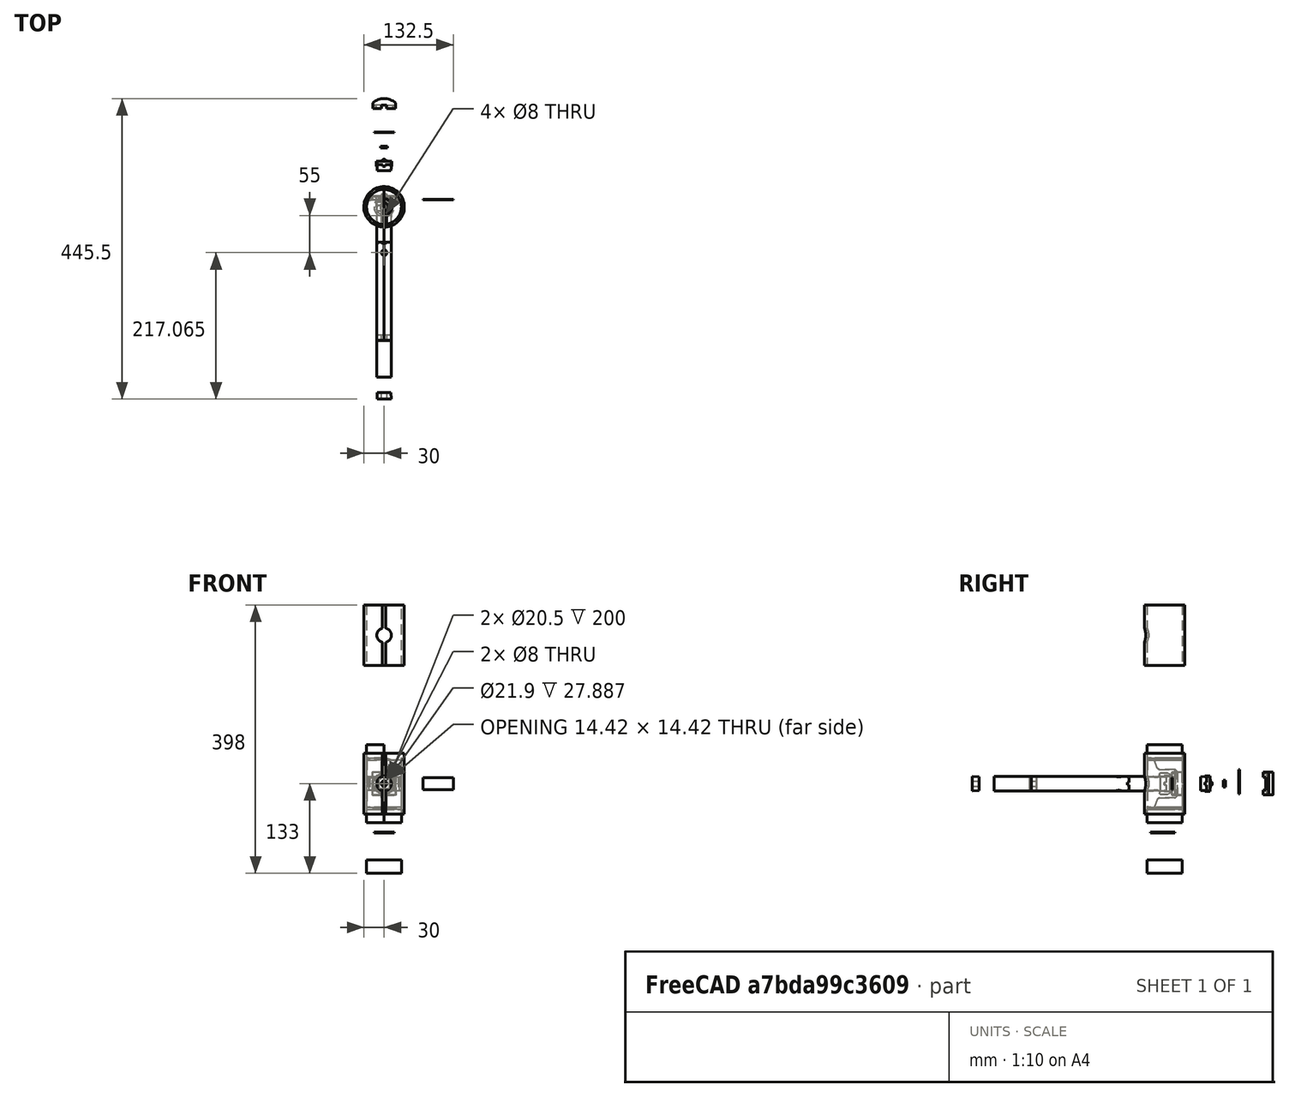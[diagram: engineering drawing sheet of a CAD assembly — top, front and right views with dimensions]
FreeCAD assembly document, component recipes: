
FREECAD ASSEMBLY — COMPONENT RECIPES ("Hammer")

This assembly document has 15 components, labeled P0..P14 below (a component is one placed body or linked part). 15 of them carry a construction recipe — the FreeCAD feature program that regenerates the part from scratch, quoted from this document or its linked companion documents; the rest are supplied as boundary geometry only. No exploded tour is included for this assembly.
NOTE — this tour is split across 2 documents so each fits a 32k-token context. This is document 1: the component sections continue in the remaining 1 document, each repeating the header above.
COMPONENT P0 — recipe-attached ("Body001_CutLink", modeled in this document).
Construction recipe (the document's own serialized feature program — sketch geometry with constraints, then the solid features built on it; lengths are millimeters unless a unit is written):

FEATURE [Sketcher::SketchObject] Sketch005  label="top_sens_base"
  FullyConstrained = true
  MapMode = 5
  Support = -> [XY_Plane]
  expr: Constraints[18] = <<Properties>>.Clearance
  expr: Constraints[1] = <<Properties>>.Head_ID
  expr: Constraints[3] = 34 - <<Properties>>.Clearance * 2
  expr: Constraints[6] = 10.5 + <<Properties>>.Clearance
  sketch-geometry (8):
    g0: Circle CenterX=0 CenterY=0 CenterZ=0 NormalX=0 NormalY=0 NormalZ=1 AngleXU=0 Radius=25.7
    g1: LineSegment StartX=-16.8 StartY=10.7 StartZ=0 EndX=16.8 EndY=10.7 EndZ=0
    g2: GeomPoint X=0 Y=10.7 Z=0
    g3: LineSegment StartX=-16.8 StartY=10.7 StartZ=0 EndX=-16.8 EndY=19.1836 EndZ=0
    g4: LineSegment StartX=16.8 StartY=10.7 StartZ=0 EndX=16.8 EndY=19.1836 EndZ=0
    g5: GeomPoint X=0 Y=25.7 Z=0
    g6: ArcOfCircle CenterX=0 CenterY=0 CenterZ=0 NormalX=0 NormalY=0 NormalZ=1 AngleXU=0 Radius=25.5 StartAngle=0.851542 EndAngle=2.29005
    g7: GeomPoint X=0 Y=25.5 Z=0
  constraints (19):
    c: Coincident(g0,g-1)
    c: Diameter(g0) = 51.4
    c: Horizontal(g1)
    c: DistanceX(g1,g1) = 33.6
    c: Symmetric(g1,g1,g2)
    c: PointOnObject(g2,g-2)
    c: DistanceY(g0,g2) = 10.7
    c: Coincident(g3,g1)
    c: Vertical(g3)
    c: Vertical(g4)
    c: Coincident(g4,g1)
    c: PointOnObject(g5,g0)
    c: PointOnObject(g5,g-2)
    c: Coincident(g6,g0)
    c: Coincident(g6,g3)
    c: Coincident(g6,g4)
    c: PointOnObject(g7,g6)
    c: PointOnObject(g7,g-2)
    c: DistanceY(g7,g5) = 0.2
FEATURE [PartDesign::Pad] Pad001  label="Top_Base"
  Direction = (0,0,1)
  Length = 16.8
  Length2 = 16.8
  Profile = -> Sketch005
  ReferenceAxis = -> Sketch005 [N_Axis]
  Type = 4
  expr: Length = <<Properties>>.Sensor_Diameter / 2 + 2 - <<Properties>>.Clearance
  expr: Length2 = <<Properties>>.Sensor_Diameter / 2 + 2 - <<Properties>>.Clearance
FEATURE [Sketcher::SketchObject] Sketch006
  FullyConstrained = true
  MapMode = 5
  Support = -> [XY_Plane]
  expr: Constraints[1] = Sketch003.Constraints[1]
  expr: Constraints[22] = Sketch003.Constraints[22]
  expr: Constraints[23] = Sketch003.Constraints[23]
  expr: Constraints[33] = Sketch003.Constraints[33]
  expr: Constraints[35] = Sketch003.Constraints[35]
  expr: Constraints[38] = Sketch003.Constraints[38]
  expr: Constraints[3] = Sketch003.Constraints[3]
  expr: Constraints[7] = Sketch003.Constraints[7]
  sketch-geometry (15):
    g0: Circle CenterX=0 CenterY=0 CenterZ=0 NormalX=0 NormalY=0 NormalZ=1 AngleXU=0 Radius=25.7
    g1: LineSegment StartX=-15.2 StartY=15.4669 StartZ=0 EndX=15.2 EndY=15.4669 EndZ=0
    g2: GeomPoint X=0 Y=15.4669 Z=0
    g3: LineSegment StartX=-23 StartY=11.4669 StartZ=0 EndX=23 EndY=11.4669 EndZ=0
    g4: GeomPoint X=0 Y=11.4669 Z=0
    g5: LineSegment StartX=-15.2 StartY=15.4669 StartZ=0 EndX=-21 EndY=11.4669 EndZ=0
    g6: LineSegment StartX=15.2 StartY=15.4669 StartZ=0 EndX=21 EndY=11.4669 EndZ=0
    g7: LineSegment StartX=21 StartY=11.4669 StartZ=0 EndX=23 EndY=11.4669 EndZ=0
    g8: LineSegment StartX=-21 StartY=11.4669 StartZ=0 EndX=-23 EndY=11.4669 EndZ=0
    g9: ArcOfCircle CenterX=0 CenterY=0 CenterZ=0 NormalX=0 NormalY=0 NormalZ=1 AngleXU=0 Radius=25.7 StartAngle=2.6791 EndAngle=2.80587
    g10: ArcOfCircle CenterX=0 CenterY=0 CenterZ=0 NormalX=0 NormalY=0 NormalZ=1 AngleXU=0 Radius=25.7 StartAngle=0.335723 EndAngle=0.462496
    g11: LineSegment StartX=-11 StartY=10.5 StartZ=0 EndX=-24.2652 EndY=8.46691 EndZ=0
    g12: LineSegment StartX=11 StartY=10.5 StartZ=0 EndX=24.2652 EndY=8.46691 EndZ=0
    g13: LineSegment StartX=11 StartY=10.5 StartZ=0 EndX=-11 EndY=10.5 EndZ=0
    g14: GeomPoint X=0 Y=10.5 Z=0
  constraints (40):
    c: Coincident(g0,g-1)
    c: Diameter(g0) = 51.4
    c: Horizontal(g1)
    c: DistanceX(g1,g1) = 30.4
    c: Symmetric(g1,g1,g2)
    c: PointOnObject(g2,g-2)
    c: Horizontal(g3)
    c: DistanceX(g3,g3) = 46
    c: Symmetric(g3,g3,g4)
    c: PointOnObject(g4,g-2)
    c: Coincident(g5,g1)
    c: PointOnObject(g5,g3)
    c: Coincident(g6,g1)
    c: PointOnObject(g6,g3)
    c: Coincident(g7,g6)
    c: PointOnObject(g7,g0)
    c: Horizontal(g7)
    c: Coincident(g8,g5)
    c: PointOnObject(g8,g0)
    c: Horizontal(g8)
    c: Equal(g8,g7)
    c: PointOnObject(g3,g0)
    c: DistanceY(g6,g1) = 4
    c: DistanceX(g6,g7) = 2
    c: Coincident(g9,g0)
    c: Coincident(g9,g8)
    c: Coincident(g10,g9)
    c: Coincident(g10,g7)
    c: Coincident(g13,g12)
    c: Coincident(g13,g11)
    c: Horizontal(g13)
    c: Coincident(g10,g12)
    c: Coincident(g9,g11)
    c: DistanceX(g12,g6) = 10
    c: Equal(g12,g11)
    c: DistanceY(g10,g7) = 3
    c: Symmetric(g13,g13,g14)
    c: PointOnObject(g14,g-2)
    c: DistanceY(g9,g14) = 10.5
    c: DistanceY(g9,g2) = 15.4669
FEATURE [PartDesign::Pocket] Pocket004
  BaseFeature = -> Pad001
  Direction = (0,0,-1)
  Length = 9.5
  Length2 = 9.5
  Profile = -> Sketch006
  ReferenceAxis = -> Sketch006 [N_Axis]
  Type = 4
FEATURE [PartDesign::Chamfer] Chamfer002
  Angle = 45
  Base = -> Pocket004 [Edge22,Edge12]
  BaseFeature = -> Pocket004
  ChamferType = 0
  FlipDirection = false
  Size = 0.3
  Size2 = 1
  SupportTransform = false
  UseAllEdges = false
FEATURE [Sketcher::SketchObject] Sketch007
  FullyConstrained = true
  MapMode = 5
  Placement = pos=(0,0,0) rot=(1,0,0;1.5708rad)
  Support = -> [XZ_Plane]
  expr: Constraints[11] = <<Properties>>.Sensor_Wire_Track_Width
  expr: Constraints[1] = <<Properties>>.Sensor_Diameter + 1
  expr: Constraints[27] = <<Properties>>.Sensor_Wire_Track_Width
  sketch-geometry (11):
    g0: Circle CenterX=0 CenterY=0 CenterZ=0 NormalX=0 NormalY=0 NormalZ=1 AngleXU=0 Radius=15.5
    g1: LineSegment StartX=-4 StartY=14.975 StartZ=0 EndX=-4 EndY=27.305 EndZ=0
    g2: LineSegment StartX=-4 StartY=27.305 StartZ=0 EndX=4 EndY=27.305 EndZ=0
    g3: LineSegment StartX=4 StartY=27.305 StartZ=0 EndX=4 EndY=14.975 EndZ=0
    g4: GeomPoint X=0 Y=27.305 Z=0
    g5: LineSegment StartX=-4 StartY=-14.975 StartZ=0 EndX=-4 EndY=-27.305 EndZ=0
    g6: LineSegment StartX=-4 StartY=-27.305 StartZ=0 EndX=4 EndY=-27.305 EndZ=0
    g7: LineSegment StartX=4 StartY=-27.305 StartZ=0 EndX=4 EndY=-14.975 EndZ=0
    g8: GeomPoint X=0 Y=-27.305 Z=0
    g9: ArcOfCircle CenterX=0 CenterY=0 CenterZ=0 NormalX=0 NormalY=0 NormalZ=1 AngleXU=0 Radius=15.5 StartAngle=1.83181 EndAngle=4.45137
    g10: ArcOfCircle CenterX=0 CenterY=0 CenterZ=0 NormalX=0 NormalY=0 NormalZ=1 AngleXU=0 Radius=15.5 StartAngle=4.97341 EndAngle=7.59296
  constraints (28):
    c: Coincident(g0,g-1)
    c: Diameter(g0) = 31
    c: PointOnObject(g1,g0)
    c: Vertical(g1)
    c: Coincident(g2,g1)
    c: Horizontal(g2)
    c: Coincident(g3,g2)
    c: PointOnObject(g3,g0)
    c: Vertical(g3)
    c: Symmetric(g2,g2,g4)
    c: PointOnObject(g4,g-2)
    c: DistanceX(g2,g2) = 8
    c: DistanceY(g3,g3) = 12.33
    c: Vertical(g5)
    c: Coincident(g6,g5)
    c: Horizontal(g6)
    c: Coincident(g7,g6)
    c: Vertical(g7)
    c: Symmetric(g6,g6,g8)
    c: PointOnObject(g8,g-2)
    c: Equal(g7,g3)
    c: Coincident(g9,g0)
    c: Coincident(g9,g1)
    c: Coincident(g9,g5)
    c: Coincident(g10,g9)
    c: Coincident(g10,g3)
    c: Coincident(g10,g7)
    c: DistanceX(g6,g6) = 8
FEATURE [PartDesign::Pocket] Pocket005
  BaseFeature = -> Chamfer002
  Direction = (0,1,2e-16)
  Length = 0
  Length2 = 5
  Offset = 0.4
  Profile = -> Sketch007
  ReferenceAxis = -> Sketch007 [N_Axis]
  Type = 3
  UpToFace = -> Chamfer002 [Face11]
FEATURE [PartDesign::Body] Body001  label="TopSensor"
  Group = -> [Sketch005,Pad001,Sketch006,Pocket004,Chamfer002,Sketch007,Pocket005]
  Origin = -> Origin
  Tip = -> Pocket005
COMPONENT P1 — recipe-attached ("Body002_CutLink", modeled in this document).
Construction recipe (the document's own serialized feature program — sketch geometry with constraints, then the solid features built on it; lengths are millimeters unless a unit is written):

FEATURE [Sketcher::SketchObject] Sketch009
  FullyConstrained = true
  MapMode = 5
  Support = -> [XY_Plane002]
  sketch-geometry (2):
    g0: Circle CenterX=0 CenterY=0 CenterZ=0 NormalX=0 NormalY=0 NormalZ=1 AngleXU=0 Radius=26
    g1: Circle CenterX=0 CenterY=0 CenterZ=0 NormalX=0 NormalY=0 NormalZ=1 AngleXU=0 Radius=30
  constraints (4):
    c: Coincident(g0,g-1)
    c: Coincident(g1,g0)
    c: Diameter(g0) = 52
    c: Diameter(g1) = 60
FEATURE [PartDesign::Pad] Pad002
  Direction = (0,0,1)
  Length = 45
  Length2 = 45
  Profile = -> Sketch009
  ReferenceAxis = -> Sketch009 [N_Axis]
  Type = 4
FEATURE [Sketcher::SketchObject] Sketch010
  FullyConstrained = true
  MapMode = 5
  Placement = pos=(0,0,0) rot=(1,0,0;1.5708rad)
  Support = -> [XZ_Plane002]
  expr: Constraints[1] = <<Properties>>.Handle_OD
  sketch-geometry (1):
    g0: Circle CenterX=0 CenterY=0 CenterZ=0 NormalX=0 NormalY=0 NormalZ=1 AngleXU=0 Radius=10.75
  constraints (2):
    c: Coincident(g0,g-1)
    c: Diameter(g0) = 21.5
FEATURE [PartDesign::Pocket] Pocket007
  BaseFeature = -> Pad002
  Direction = (0,1,2e-16)
  Length = 5
  Length2 = 5
  Profile = -> Sketch010
  ReferenceAxis = -> Sketch010 [N_Axis]
  Reversed = true
  Type = 1
FEATURE [Sketcher::SketchObject] Sketch027
  FullyConstrained = true
  MapMode = 5
  Placement = pos=(0,0,0) rot=(1,0,0;1.5708rad)
  Support = -> [XZ_Plane002]
  sketch-geometry (5):
    g0: LineSegment StartX=-2.5 StartY=-45 StartZ=0 EndX=-2.5 EndY=45 EndZ=0
    g1: LineSegment StartX=-2.5 StartY=45 StartZ=0 EndX=2.5 EndY=45 EndZ=0
    g2: LineSegment StartX=2.5 StartY=45 StartZ=0 EndX=2.5 EndY=-45 EndZ=0
    g3: LineSegment StartX=2.5 StartY=-45 StartZ=0 EndX=-2.5 EndY=-45 EndZ=0
    g4: GeomPoint X=0 Y=0 Z=0
  constraints (12):
    c: Coincident(g0,g1)
    c: Coincident(g1,g2)
    c: Coincident(g2,g3)
    c: Coincident(g3,g0)
    c: Horizontal(g1)
    c: Horizontal(g3)
    c: Vertical(g0)
    c: Vertical(g2)
    c: Symmetric(g1,g0,g4)
    c: Coincident(g4,g-1)
    c: DistanceX(g1,g1) = 5
    c: DistanceY(g2,g2) = 90
FEATURE [PartDesign::Pocket] Pocket012
  BaseFeature = -> Pocket007
  Direction = (0,1,2e-16)
  Length = 5
  Length2 = 5
  Profile = -> Sketch027
  ReferenceAxis = -> Sketch027 [N_Axis]
  Reversed = true
  Type = 1
FEATURE [PartDesign::Body] Body002  label="PVCHammerHeadShell"
  Group = -> [Sketch009,Pad002,Sketch010,Pocket007,Sketch027,Pocket012]
  Origin = -> Origin002
  Tip = -> Pocket012
COMPONENT P2 — recipe-attached ("Body003_CutLink", modeled in this document).
Construction recipe (the document's own serialized feature program — sketch geometry with constraints, then the solid features built on it; lengths are millimeters unless a unit is written):

FEATURE [Sketcher::SketchObject] Sketch011
  FullyConstrained = true
  MapMode = 5
  Placement = pos=(0,0,0) rot=(1,0,0;1.5708rad)
  Support = -> [XZ_Plane003]
  expr: Constraints[3] = <<Properties>>.Handle_ID
  sketch-geometry (2):
    g0: Circle CenterX=0 CenterY=0 CenterZ=0 NormalX=0 NormalY=0 NormalZ=1 AngleXU=0 Radius=10.625
    g1: Circle CenterX=0 CenterY=0 CenterZ=0 NormalX=0 NormalY=0 NormalZ=1 AngleXU=0 Radius=10.25
  constraints (4):
    c: Coincident(g0,g-1)
    c: Diameter(g0) = 21.25
    c: Coincident(g1,g0)
    c: Diameter(g1) = 20.5
FEATURE [PartDesign::Pad] Pad003
  Direction = (0,-1,-2e-16)
  Length = 200
  Length2 = 10
  Placement = pos=(0,0,0) rot=(1,0,0;1.5708rad)
  Profile = -> Sketch011
  ReferenceAxis = -> Sketch011 [N_Axis]
  Type = 0
FEATURE [Sketcher::SketchObject] Sketch018
  FullyConstrained = false
  MapMode = 5
  Support = -> [XY_Plane003]
  sketch-geometry (1):
    g0: Circle CenterX=0 CenterY=-15.4348 CenterZ=0 NormalX=0 NormalY=0 NormalZ=1 AngleXU=0 Radius=4
  constraints (2):
    c: PointOnObject(g0,g-2)
    c: Diameter(g0) = 8
FEATURE [PartDesign::Pocket] Pocket008
  BaseFeature = -> Pad003
  Direction = (0,0,-1)
  Length = 50
  Length2 = 50
  Placement = pos=(0,0,0) rot=(1,0,0;1.5708rad)
  Profile = -> Sketch018
  ReferenceAxis = -> Sketch018 [N_Axis]
  Type = 4
FEATURE [Sketcher::SketchObject] Sketch019
  FullyConstrained = true
  MapMode = 5
  Placement = pos=(0,0,0) rot=(1,0,0;1.5708rad)
  Support = -> [XZ_Plane003]
  sketch-geometry (17):
    g0: LineSegment StartX=12 StartY=-2 StartZ=0 EndX=12 EndY=2 EndZ=0
    g1: LineSegment StartX=12 StartY=2 StartZ=0 EndX=2 EndY=2 EndZ=0
    g2: LineSegment StartX=2 StartY=2 StartZ=0 EndX=2 EndY=12 EndZ=0
    g3: LineSegment StartX=2 StartY=12 StartZ=0 EndX=-2 EndY=12 EndZ=0
    g4: LineSegment StartX=-2 StartY=12 StartZ=0 EndX=-2 EndY=2 EndZ=0
    g5: LineSegment StartX=-2 StartY=2 StartZ=0 EndX=-12 EndY=2 EndZ=0
    g6: LineSegment StartX=-12 StartY=2 StartZ=0 EndX=-12 EndY=-2 EndZ=0
    g7: LineSegment StartX=-12 StartY=-2 StartZ=0 EndX=-2 EndY=-2 EndZ=0
    g8: LineSegment StartX=-2 StartY=-2 StartZ=0 EndX=-2 EndY=-12 EndZ=0
    g9: LineSegment StartX=-2 StartY=-12 StartZ=0 EndX=2 EndY=-12 EndZ=0
    g10: LineSegment StartX=2 StartY=-12 StartZ=0 EndX=2 EndY=-2 EndZ=0
    g11: LineSegment StartX=2 StartY=-2 StartZ=0 EndX=12 EndY=-2 EndZ=0
    g12: LineSegment StartX=-2 StartY=-2 StartZ=0 EndX=-2 EndY=2 EndZ=0
    g13: LineSegment StartX=-2 StartY=2 StartZ=0 EndX=2 EndY=2 EndZ=0
    g14: LineSegment StartX=2 StartY=2 StartZ=0 EndX=2 EndY=-2 EndZ=0
    g15: LineSegment StartX=2 StartY=-2 StartZ=0 EndX=-2 EndY=-2 EndZ=0
    g16: GeomPoint X=0 Y=0 Z=0
  constraints (46):
    c: Vertical(g0)
    c: Coincident(g1,g0)
    c: Horizontal(g1)
    c: Coincident(g2,g1)
    c: Vertical(g2)
    c: Coincident(g3,g2)
    c: Horizontal(g3)
    c: Coincident(g4,g3)
    c: Vertical(g4)
    c: Coincident(g5,g4)
    c: Horizontal(g5)
    c: Coincident(g6,g5)
    c: Vertical(g6)
    c: Horizontal(g7)
    c: Coincident(g8,g7)
    c: Vertical(g8)
    c: Horizontal(g9)
    c: Coincident(g10,g9)
    c: Vertical(g10)
    c: Coincident(g11,g10)
    c: Coincident(g11,g0)
    c: Horizontal(g11)
    c: Equal(g0,g3)
    c: Equal(g3,g6)
    c: Equal(g6,g9)
    c: Coincident(g6,g7)
    c: Coincident(g9,g8)
    c: Equal(g11,g7)
    c: Equal(g11,g1)
    c: Equal(g2,g4)
    c: Equal(g5,g10)
    c: Coincident(g12,g13)
    c: Coincident(g13,g14)
    c: Coincident(g14,g15)
    c: Coincident(g15,g12)
    c: Horizontal(g13)
    c: Horizontal(g15)
    c: Vertical(g12)
    c: Vertical(g14)
    c: Symmetric(g13,g12,g16)
    c: Coincident(g16,g-1)
    c: Coincident(g13,g1)
    c: Coincident(g7,g12)
    c: DistanceX(g13,g13) = 4
    c: DistanceY(g2,g2) = 10
    c: Equal(g10,g2)
FEATURE [PartDesign::Pocket] Pocket009
  BaseFeature = -> Pocket008
  Direction = (0,1,2e-16)
  Length = 3
  Length2 = 5
  Placement = pos=(0,0,0) rot=(1,0,0;1.5708rad)
  Profile = -> Sketch019
  ReferenceAxis = -> Sketch019 [N_Axis]
  Reversed = true
  Type = 0
FEATURE [PartDesign::Body] Body003  label="MetalHandle"
  Group = -> [Sketch011,Pad003,Sketch018,Pocket008,Sketch019,Pocket009]
  Origin = -> Origin003
  Placement = pos=(0,2.5,0) rot=(0,0,1;0rad)
  Tip = -> Pocket009
COMPONENT P3 — recipe-attached ("Body005_CutLink", modeled in this document).
Construction recipe (the document's own serialized feature program — sketch geometry with constraints, then the solid features built on it; lengths are millimeters unless a unit is written):

FEATURE [Sketcher::SketchObject] Sketch014
  FullyConstrained = true
  MapMode = 5
  Support = -> [XY_Plane005]
  sketch-geometry (5):
    g0: ArcOfCircle CenterX=0 CenterY=0 CenterZ=0 NormalX=0 NormalY=0 NormalZ=1 AngleXU=0 Radius=15 StartAngle=4.90695 EndAngle=10.801
    g1: LineSegment StartX=2.9 StartY=-14.717 StartZ=0 EndX=2.9 EndY=-20.717 EndZ=0
    g2: LineSegment StartX=2.9 StartY=-20.717 StartZ=0 EndX=-2.9 EndY=-20.717 EndZ=0
    g3: LineSegment StartX=-2.9 StartY=-20.717 StartZ=0 EndX=-2.9 EndY=-14.717 EndZ=0
    g4: LineSegment StartX=2.9 StartY=-14.717 StartZ=0 EndX=-2.9 EndY=-14.717 EndZ=0
  constraints (14):
    c: Coincident(g0,g-1)
    c: Radius(g0) = 15
    c: Coincident(g1,g0)
    c: Vertical(g1)
    c: Coincident(g2,g1)
    c: Horizontal(g2)
    c: Coincident(g3,g2)
    c: Coincident(g3,g0)
    c: Vertical(g3)
    c: DistanceX(g2,g2) = 5.8
    c: Coincident(g4,g0)
    c: Coincident(g4,g0)
    c: Horizontal(g4)
    c: DistanceY(g1,g1) = 6
FEATURE [PartDesign::Pad] Pad007
  Direction = (0,0,1)
  Length = 1
  Length2 = 10
  Profile = -> Sketch014
  ReferenceAxis = -> Sketch014 [N_Axis]
  Type = 0
FEATURE [PartDesign::Body] Body005  label="Sensor1"
  Group = -> [Sketch014,Pad007]
  Origin = -> Origin005
  Placement = pos=(0,0,37) rot=(0,0,1;0rad)
  Tip = -> Pad007
COMPONENT P4 — recipe-attached ("Body006_CutLink", modeled in this document).
Construction recipe (the document's own serialized feature program — sketch geometry with constraints, then the solid features built on it; lengths are millimeters unless a unit is written):

FEATURE [PartDesign::FeatureBase] Clone
  BaseFeature = -> Body005
FEATURE [PartDesign::Body] Body006  label="Sensor2"
  Group = -> [Clone]
  Origin = -> Origin006
  Placement = pos=(0,0,-37) rot=(0,1,0;3.14159rad)
  Tip = -> Clone
COMPONENT P5 — recipe-attached ("Body007_CutLink", modeled in this document).
Construction recipe (the document's own serialized feature program — sketch geometry with constraints, then the solid features built on it; lengths are millimeters unless a unit is written):

FEATURE [PartDesign::FeatureBase] Clone001
  BaseFeature = -> Body005
FEATURE [PartDesign::Body] Body007  label="Sensor3"
  Group = -> [Clone001]
  Origin = -> Origin007
  Placement = pos=(0,16,-4e-15) rot=(0,0.707107,-0.707107;3.14159rad)
  Tip = -> Clone001
COMPONENT P6 — recipe-attached ("Body008_CutLink", modeled in this document).
Construction recipe (the document's own serialized feature program — sketch geometry with constraints, then the solid features built on it; lengths are millimeters unless a unit is written):

FEATURE [Sketcher::SketchObject] Sketch015
  FullyConstrained = true
  MapMode = 5
  Support = -> [XY_Plane008]
  sketch-geometry (1):
    g0: Circle CenterX=0 CenterY=0 CenterZ=0 NormalX=0 NormalY=0 NormalZ=1 AngleXU=0 Radius=26
  constraints (2):
    c: Coincident(g0,g-1)
    c: Diameter(g0) = 52
FEATURE [PartDesign::Pad] Pad008
  Direction = (0,0,1)
  Length = 20
  Length2 = 10
  Profile = -> Sketch015
  ReferenceAxis = -> Sketch015 [N_Axis]
  Type = 0
FEATURE [PartDesign::Body] Body008  label="Foam1"
  Group = -> [Sketch015,Pad008]
  Origin = -> Origin008
  Placement = pos=(0,0,38) rot=(0,0,1;0rad)
  Tip = -> Pad008
COMPONENT P7 — recipe-attached ("Body009_CutLink", modeled in this document).
Construction recipe (the document's own serialized feature program — sketch geometry with constraints, then the solid features built on it; lengths are millimeters unless a unit is written):

FEATURE [PartDesign::FeatureBase] Clone002
  BaseFeature = -> Body008
  Placement = pos=(0,0,38) rot=(0,0,1;0rad)
FEATURE [PartDesign::Body] Body009  label="Foam2"
  Group = -> [Clone002]
  Origin = -> Origin009
  Placement = pos=(0,0,0) rot=(1,0,0;3.14159rad)
  Tip = -> Clone002
COMPONENT P8 — recipe-attached ("Body010_CutLink", modeled in this document).
Construction recipe (the document's own serialized feature program — sketch geometry with constraints, then the solid features built on it; lengths are millimeters unless a unit is written):

FEATURE [Sketcher::SketchObject] Sketch016
  FullyConstrained = true
  MapMode = 5
  Support = -> [XY_Plane010]
  sketch-geometry (5):
    g0: LineSegment StartX=-22.5 StartY=-0.4 StartZ=0 EndX=-22.5 EndY=0.4 EndZ=0
    g1: LineSegment StartX=-22.5 StartY=0.4 StartZ=0 EndX=22.5 EndY=0.4 EndZ=0
    g2: LineSegment StartX=22.5 StartY=0.4 StartZ=0 EndX=22.5 EndY=-0.4 EndZ=0
    g3: LineSegment StartX=22.5 StartY=-0.4 StartZ=0 EndX=-22.5 EndY=-0.4 EndZ=0
    g4: GeomPoint X=0 Y=0 Z=0
  constraints (12):
    c: Coincident(g0,g1)
    c: Coincident(g1,g2)
    c: Coincident(g2,g3)
    c: Coincident(g3,g0)
    c: Horizontal(g1)
    c: Horizontal(g3)
    c: Vertical(g0)
    c: Vertical(g2)
    c: Symmetric(g1,g0,g4)
    c: Coincident(g4,g-1)
    c: DistanceX(g1,g1) = 45
    c: DistanceY(g2,g2) = 0.8
FEATURE [PartDesign::Pad] Pad009
  Direction = (0,0,1)
  Length = 9
  Length2 = 9
  Profile = -> Sketch016
  ReferenceAxis = -> Sketch016 [N_Axis]
  Type = 4
FEATURE [PartDesign::Body] Body010  label="ShimStock"
  Group = -> [Sketch016,Pad009]
  Origin = -> Origin010
  Placement = pos=(0,11,0) rot=(0,0,1;0rad)
  Tip = -> Pad009
COMPONENT P9 — recipe-attached ("Body011_CutLink", modeled in this document).
Construction recipe (the document's own serialized feature program — sketch geometry with constraints, then the solid features built on it; lengths are millimeters unless a unit is written):

FEATURE [Sketcher::SketchObject] Sketch017
  FullyConstrained = true
  MapMode = 5
  Placement = pos=(0,0,0) rot=(1,0,0;1.5708rad)
  Support = -> [XZ_Plane011]
  sketch-geometry (1):
    g0: Circle CenterX=0 CenterY=0 CenterZ=0 NormalX=0 NormalY=0 NormalZ=1 AngleXU=0 Radius=5
  constraints (2):
    c: Coincident(g0,g-1)
    c: Diameter(g0) = 10
FEATURE [PartDesign::Pad] Pad010
  Direction = (0,-1,-2e-16)
  Length = 3
  Length2 = 10
  Placement = pos=(0,0,0) rot=(1,0,0;1.5708rad)
  Profile = -> Sketch017
  ReferenceAxis = -> Sketch017 [N_Axis]
  Type = 0
FEATURE [PartDesign::Body] Body011  label="TopFoam"
  Group = -> [Sketch017,Pad010]
  Origin = -> Origin011
  Placement = pos=(0,15,0) rot=(0,0,1;0rad)
  Tip = -> Pad010
COMPONENT P10 — recipe-attached ("Body012_CutLink", modeled in this document).
Construction recipe (the document's own serialized feature program — sketch geometry with constraints, then the solid features built on it; lengths are millimeters unless a unit is written):

FEATURE [Sketcher::SketchObject] Sketch020
  FullyConstrained = true
  MapMode = 5
  Placement = pos=(0,0,0) rot=(1,0,0;1.5708rad)
  Support = -> [XZ_Plane012]
  expr: Constraints[43] = Sketch019.Constraints[43]
  expr: Constraints[44] = Sketch019.Constraints[44]
  expr: Constraints[77] = <<Properties>>.Clearance
  expr: Constraints[78] = <<Properties>>.Clearance
  expr: Constraints[79] = <<Properties>>.Clearance
  expr: Constraints[81] = (<<Properties>>.Handle_OD + 2) / 2 - <<Properties>>.Clearance
  sketch-geometry (29):
    g0: LineSegment StartX=12 StartY=-2 StartZ=0 EndX=12 EndY=2 EndZ=0
    g1: LineSegment StartX=12 StartY=2 StartZ=0 EndX=2 EndY=2 EndZ=0
    g2: LineSegment StartX=2 StartY=2 StartZ=0 EndX=2 EndY=12 EndZ=0
    g3: LineSegment StartX=2 StartY=12 StartZ=0 EndX=-2 EndY=12 EndZ=0
    g4: LineSegment StartX=-2 StartY=12 StartZ=0 EndX=-2 EndY=2 EndZ=0
    g5: LineSegment StartX=-2 StartY=2 StartZ=0 EndX=-12 EndY=2 EndZ=0
    g6: LineSegment StartX=-12 StartY=2 StartZ=0 EndX=-12 EndY=-2 EndZ=0
    g7: LineSegment StartX=-12 StartY=-2 StartZ=0 EndX=-2 EndY=-2 EndZ=0
    g8: LineSegment StartX=-2 StartY=-2 StartZ=0 EndX=-2 EndY=-12 EndZ=0
    g9: LineSegment StartX=-2 StartY=-12 StartZ=0 EndX=2 EndY=-12 EndZ=0
    g10: LineSegment StartX=2 StartY=-12 StartZ=0 EndX=2 EndY=-2 EndZ=0
    g11: LineSegment StartX=2 StartY=-2 StartZ=0 EndX=12 EndY=-2 EndZ=0
    g12: LineSegment StartX=-2 StartY=-2 StartZ=0 EndX=-2 EndY=2 EndZ=0
    g13: LineSegment StartX=-2 StartY=2 StartZ=0 EndX=2 EndY=2 EndZ=0
    g14: LineSegment StartX=2 StartY=2 StartZ=0 EndX=2 EndY=-2 EndZ=0
    g15: LineSegment StartX=2 StartY=-2 StartZ=0 EndX=-2 EndY=-2 EndZ=0
    g16: GeomPoint X=0 Y=0 Z=0
    g17: LineSegment StartX=-1.8 StartY=11.55 StartZ=0 EndX=-1.8 EndY=1.8 EndZ=0
    g18: LineSegment StartX=-1.8 StartY=1.8 StartZ=0 EndX=-11.55 EndY=1.8 EndZ=0
    g19: LineSegment StartX=-11.55 StartY=1.8 StartZ=0 EndX=-11.55 EndY=-1.8 EndZ=0
    g20: LineSegment StartX=-11.55 StartY=-1.8 StartZ=0 EndX=-1.8 EndY=-1.8 EndZ=0
    g21: LineSegment StartX=-1.8 StartY=-1.8 StartZ=0 EndX=-1.8 EndY=-11.55 EndZ=0
    g22: LineSegment StartX=-1.8 StartY=-11.55 StartZ=0 EndX=1.8 EndY=-11.55 EndZ=0
    g23: LineSegment StartX=1.8 StartY=-11.55 StartZ=0 EndX=1.8 EndY=-1.8 EndZ=0
    g24: LineSegment StartX=1.8 StartY=-1.8 StartZ=0 EndX=11.55 EndY=-1.8 EndZ=0
    g25: LineSegment StartX=11.55 StartY=-1.8 StartZ=0 EndX=11.55 EndY=1.8 EndZ=0
    g26: LineSegment StartX=11.55 StartY=1.8 StartZ=0 EndX=1.8 EndY=1.8 EndZ=0
    g27: LineSegment StartX=1.8 StartY=1.8 StartZ=0 EndX=1.8 EndY=11.55 EndZ=0
    g28: LineSegment StartX=1.8 StartY=11.55 StartZ=0 EndX=-1.8 EndY=11.55 EndZ=0
  constraints (82):
    c: Vertical(g0)
    c: Coincident(g1,g0)
    c: Horizontal(g1)
    c: Coincident(g2,g1)
    c: Vertical(g2)
    c: Coincident(g3,g2)
    c: Horizontal(g3)
    c: Coincident(g4,g3)
    c: Vertical(g4)
    c: Coincident(g5,g4)
    c: Horizontal(g5)
    c: Coincident(g6,g5)
    c: Vertical(g6)
    c: Horizontal(g7)
    c: Coincident(g8,g7)
    c: Vertical(g8)
    c: Horizontal(g9)
    c: Coincident(g10,g9)
    c: Vertical(g10)
    c: Coincident(g11,g10)
    c: Coincident(g11,g0)
    c: Horizontal(g11)
    c: Equal(g0,g3)
    c: Equal(g3,g6)
    c: Equal(g6,g9)
    c: Coincident(g6,g7)
    c: Coincident(g9,g8)
    c: Equal(g11,g7)
    c: Equal(g11,g1)
    c: Equal(g2,g4)
    c: Equal(g5,g10)
    c: Coincident(g12,g13)
    c: Coincident(g13,g14)
    c: Coincident(g14,g15)
    c: Coincident(g15,g12)
    c: Horizontal(g13)
    c: Horizontal(g15)
    c: Vertical(g12)
    c: Vertical(g14)
    c: Symmetric(g13,g12,g16)
    c: Coincident(g16,g-1)
    c: Coincident(g13,g1)
    c: Coincident(g7,g12)
    c: DistanceX(g13,g13) = 4
    c: DistanceY(g2,g2) = 10
    c: Equal(g10,g2)
    c: Vertical(g17)
    c: Coincident(g18,g17)
    c: Horizontal(g18)
    c: Coincident(g19,g18)
    c: Vertical(g19)
    c: Coincident(g20,g19)
    c: Horizontal(g20)
    c: Coincident(g21,g20)
    c: Vertical(g21)
    c: Coincident(g22,g21)
    c: Horizontal(g22)
    c: Coincident(g23,g22)
    c: Vertical(g23)
    c: Coincident(g24,g23)
    c: Horizontal(g24)
    c: Coincident(g25,g24)
    c: Vertical(g25)
    c: Coincident(g26,g25)
    c: Horizontal(g26)
    c: Coincident(g27,g26)
    c: Vertical(g27)
    c: Coincident(g28,g27)
    c: Coincident(g28,g17)
    c: Horizontal(g28)
    c: Equal(g26,g18)
    c: Equal(g27,g17)
    c: Equal(g26,g24)
    c: Equal(g20,g24)
    c: Equal(g21,g23)
    c: Equal(g23,g27)
    c: Equal(g22,g25)
    c: DistanceX(g26,g1) = 0.2
    c: DistanceY(g26,g1) = 0.2
    c: DistanceY(g0,g24) = 0.2
    c: Equal(g23,g24)
    c: DistanceX(g16,g25) = 11.55
FEATURE [PartDesign::Pad] Pad011
  Direction = (0,-1,2e-16)
  Length = 2.8
  Length2 = 10
  Placement = pos=(0,0,0) rot=(1,0,0;1.5708rad)
  Profile = -> Sketch020
  ReferenceAxis = -> Sketch020 [N_Axis]
  Type = 0
FEATURE [Sketcher::SketchObject] Sketch021
  FullyConstrained = true
  MapMode = 5
  Placement = pos=(0,0,0) rot=(1,0,0;1.5708rad)
  Support = -> [XZ_Plane012]
  expr: Constraints[53] = Sketch020.Constraints[43]
  expr: Constraints[54] = Sketch020.Constraints[44]
  expr: Constraints[87] = Sketch020.Constraints[77]
  expr: Constraints[88] = Sketch020.Constraints[78]
  expr: Constraints[89] = Sketch020.Constraints[79]
  expr: Constraints[91] = Sketch020.Constraints[81]
  sketch-geometry (34):
    g0: LineSegment StartX=11.55 StartY=11.55 StartZ=0 EndX=11.55 EndY=-11.55 EndZ=0
    g1: LineSegment StartX=11.55 StartY=-11.55 StartZ=0 EndX=-11.55 EndY=-11.55 EndZ=0
    g2: LineSegment StartX=-11.55 StartY=-11.55 StartZ=0 EndX=-11.55 EndY=11.55 EndZ=0
    g3: LineSegment StartX=-11.55 StartY=11.55 StartZ=0 EndX=11.55 EndY=11.55 EndZ=0
    g4: GeomPoint X=0 Y=0 Z=0
    g5: LineSegment StartX=12 StartY=-2 StartZ=0 EndX=12 EndY=2 EndZ=0
    g6: LineSegment StartX=12 StartY=2 StartZ=0 EndX=2 EndY=2 EndZ=0
    g7: LineSegment StartX=2 StartY=2 StartZ=0 EndX=2 EndY=12 EndZ=0
    g8: LineSegment StartX=2 StartY=12 StartZ=0 EndX=-2 EndY=12 EndZ=0
    g9: LineSegment StartX=-2 StartY=12 StartZ=0 EndX=-2 EndY=2 EndZ=0
    g10: LineSegment StartX=-2 StartY=2 StartZ=0 EndX=-12 EndY=2 EndZ=0
    g11: LineSegment StartX=-12 StartY=2 StartZ=0 EndX=-12 EndY=-2 EndZ=0
    g12: LineSegment StartX=-12 StartY=-2 StartZ=0 EndX=-2 EndY=-2 EndZ=0
    g13: LineSegment StartX=-2 StartY=-2 StartZ=0 EndX=-2 EndY=-12 EndZ=0
    g14: LineSegment StartX=-2 StartY=-12 StartZ=0 EndX=2 EndY=-12 EndZ=0
    g15: LineSegment StartX=2 StartY=-12 StartZ=0 EndX=2 EndY=-2 EndZ=0
    g16: LineSegment StartX=2 StartY=-2 StartZ=0 EndX=12 EndY=-2 EndZ=0
    g17: LineSegment StartX=-2 StartY=-2 StartZ=0 EndX=-2 EndY=2 EndZ=0
    g18: LineSegment StartX=-2 StartY=2 StartZ=0 EndX=2 EndY=2 EndZ=0
    g19: LineSegment StartX=2 StartY=2 StartZ=0 EndX=2 EndY=-2 EndZ=0
    g20: LineSegment StartX=2 StartY=-2 StartZ=0 EndX=-2 EndY=-2 EndZ=0
    g21: GeomPoint X=0 Y=0 Z=0
    g22: LineSegment StartX=-1.8 StartY=11.55 StartZ=0 EndX=-1.8 EndY=1.8 EndZ=0
    g23: LineSegment StartX=-1.8 StartY=1.8 StartZ=0 EndX=-11.55 EndY=1.8 EndZ=0
    g24: LineSegment StartX=-11.55 StartY=1.8 StartZ=0 EndX=-11.55 EndY=-1.8 EndZ=0
    g25: LineSegment StartX=-11.55 StartY=-1.8 StartZ=0 EndX=-1.8 EndY=-1.8 EndZ=0
    g26: LineSegment StartX=-1.8 StartY=-1.8 StartZ=0 EndX=-1.8 EndY=-11.55 EndZ=0
    g27: LineSegment StartX=-1.8 StartY=-11.55 StartZ=0 EndX=1.8 EndY=-11.55 EndZ=0
    g28: LineSegment StartX=1.8 StartY=-11.55 StartZ=0 EndX=1.8 EndY=-1.8 EndZ=0
    g29: LineSegment StartX=1.8 StartY=-1.8 StartZ=0 EndX=11.55 EndY=-1.8 EndZ=0
    g30: LineSegment StartX=11.55 StartY=-1.8 StartZ=0 EndX=11.55 EndY=1.8 EndZ=0
    g31: LineSegment StartX=11.55 StartY=1.8 StartZ=0 EndX=1.8 EndY=1.8 EndZ=0
    g32: LineSegment StartX=1.8 StartY=1.8 StartZ=0 EndX=1.8 EndY=11.55 EndZ=0
    g33: LineSegment StartX=1.8 StartY=11.55 StartZ=0 EndX=-1.8 EndY=11.55 EndZ=0
  constraints (94):
    c: Coincident(g0,g1)
    c: Coincident(g1,g2)
    c: Coincident(g2,g3)
    c: Coincident(g3,g0)
    c: Horizontal(g1)
    c: Horizontal(g3)
    c: Vertical(g0)
    c: Vertical(g2)
    c: Symmetric(g1,g0,g4)
    c: Coincident(g4,g-1)
    c: Vertical(g5)
    c: Coincident(g6,g5)
    c: Horizontal(g6)
    c: Coincident(g7,g6)
    c: Vertical(g7)
    c: Coincident(g8,g7)
    c: Horizontal(g8)
    c: Coincident(g9,g8)
    c: Vertical(g9)
    c: Coincident(g10,g9)
    c: Horizontal(g10)
    c: Coincident(g11,g10)
    c: Vertical(g11)
    c: Horizontal(g12)
    c: Coincident(g13,g12)
    c: Vertical(g13)
    c: Horizontal(g14)
    c: Coincident(g15,g14)
    c: Vertical(g15)
    c: Coincident(g16,g15)
    c: Coincident(g16,g5)
    c: Horizontal(g16)
    c: Equal(g5,g8)
    c: Equal(g8,g11)
    c: Equal(g11,g14)
    c: Coincident(g11,g12)
    c: Coincident(g14,g13)
    c: Equal(g16,g12)
    c: Equal(g16,g6)
    c: Equal(g7,g9)
    c: Equal(g10,g15)
    c: Coincident(g17,g18)
    c: Coincident(g18,g19)
    c: Coincident(g19,g20)
    c: Coincident(g20,g17)
    c: Horizontal(g18)
    c: Horizontal(g20)
    c: Vertical(g17)
    c: Vertical(g19)
    c: Symmetric(g18,g17,g21)
    c: Coincident(g21,g-1)
    c: Coincident(g18,g6)
    c: Coincident(g12,g17)
    c: DistanceX(g18,g18) = 4
    c: DistanceY(g7,g7) = 10
    c: Equal(g15,g7)
    c: Vertical(g22)
    c: Coincident(g23,g22)
    c: Horizontal(g23)
    c: Coincident(g24,g23)
    c: Vertical(g24)
    c: Coincident(g25,g24)
    c: Horizontal(g25)
    c: Coincident(g26,g25)
    c: Vertical(g26)
    c: Coincident(g27,g26)
    c: Horizontal(g27)
    c: Coincident(g28,g27)
    c: Vertical(g28)
    c: Coincident(g29,g28)
    c: Horizontal(g29)
    c: Coincident(g30,g29)
    c: Vertical(g30)
    c: Coincident(g31,g30)
    c: Horizontal(g31)
    c: Coincident(g32,g31)
    c: Vertical(g32)
    c: Coincident(g33,g32)
    c: Coincident(g33,g22)
    c: Horizontal(g33)
    c: Equal(g31,g23)
    c: Equal(g32,g22)
    c: Equal(g31,g29)
    c: Equal(g25,g29)
    c: Equal(g26,g28)
    c: Equal(g28,g32)
    c: Equal(g27,g30)
    c: DistanceX(g31,g6) = 0.2
    c: DistanceY(g31,g6) = 0.2
    c: DistanceY(g5,g29) = 0.2
    c: Equal(g28,g29)
    c: DistanceX(g21,g30) = 11.55
    c: PointOnObject(g22,g3)
    c: PointOnObject(g23,g2)
FEATURE [PartDesign::Pad] Pad012
  BaseFeature = -> Pad011
  Direction = (0,-1,2e-16)
  Length = 5
  Length2 = 10
  Placement = pos=(0,0,0) rot=(1,0,0;1.5708rad)
  Profile = -> Sketch021
  ReferenceAxis = -> Sketch021 [N_Axis]
  Reversed = true
  Type = 0
FEATURE [Sketcher::SketchObject] Sketch023
  FullyConstrained = true
  MapMode = 5
  Placement = pos=(0,5,-2.2e-15) rot=(-1,0,0;1.5708rad)
  Support = -> [Pad012]
  sketch-geometry (1):
    g0: Circle CenterX=0 CenterY=0 CenterZ=0 NormalX=0 NormalY=0 NormalZ=1 AngleXU=0 Radius=2.5
  constraints (2):
    c: Coincident(g0,g-1)
    c: Diameter(g0) = 5
FEATURE [PartDesign::Pad] Pad013
  BaseFeature = -> Pad012
  Direction = (0,1,-2e-16)
  Length = 3
  Length2 = 10
  Placement = pos=(0,0,0) rot=(1,0,0;1.5708rad)
  Profile = -> Sketch023
  ReferenceAxis = -> Sketch023 [N_Axis]
  Type = 0
FEATURE [PartDesign::Fillet] Fillet
  Base = -> Pad013 [Edge51]
  BaseFeature = -> Pad013
  Placement = pos=(0,0,0) rot=(1,0,0;1.5708rad)
  Radius = 2
  SupportTransform = false
  UseAllEdges = false
FEATURE [PartDesign::Fillet] Fillet001
  Base = -> Fillet [Edge3]
  BaseFeature = -> Fillet
  Placement = pos=(0,0,0) rot=(1,0,0;1.5708rad)
  Radius = 7
  SupportTransform = false
  UseAllEdges = false
FEATURE [Sketcher::SketchObject] Sketch025
  FullyConstrained = true
  MapMode = 5
  Placement = pos=(0,0,0) rot=(1,0,0;1.5708rad)
  Support = -> [XZ_Plane012]
  expr: Constraints[1] = <<Properties>>.Handle_OD - <<Properties>>.Clearance * 2
  sketch-geometry (1):
    g0: Circle CenterX=0 CenterY=0 CenterZ=0 NormalX=0 NormalY=0 NormalZ=1 AngleXU=0 Radius=10.55
  constraints (2):
    c: Coincident(g0,g-1)
    c: Diameter(g0) = 21.1
FEATURE [PartDesign::Pad] Pad014
  BaseFeature = -> Fillet001
  Direction = (0,-1,2e-16)
  Length = 9
  Length2 = 10
  Placement = pos=(0,0,0) rot=(1,0,0;1.5708rad)
  Profile = -> Sketch025
  ReferenceAxis = -> Sketch025 [N_Axis]
  TaperAngle = -2
  Type = 0
FEATURE [PartDesign::Chamfer] Chamfer006
  Angle = 45
  Base = -> Pad014 [Edge15,Edge19,Edge10,Edge11]
  BaseFeature = -> Pad014
  ChamferType = 0
  FlipDirection = false
  Placement = pos=(0,0,0) rot=(1,0,0;1.5708rad)
  Size = 1
  Size2 = 1
  SupportTransform = false
  UseAllEdges = false
FEATURE [PartDesign::Body] Body012  label="Pusher"
  Group = -> [Sketch020,Pad011,Sketch021,Pad012,Sketch023,Pad013,Fillet,Fillet001,Sketch025,Pad014,Chamfer006]
  Origin = -> Origin012
  Placement = pos=(0,2.5,0) rot=(0,0,1;0rad)
  Tip = -> Chamfer006
COMPONENT P11 — recipe-attached ("Body013_CutLink", modeled in this document).
Construction recipe (the document's own serialized feature program — sketch geometry with constraints, then the solid features built on it; lengths are millimeters unless a unit is written):

FEATURE [Sketcher::SketchObject] Sketch026
  FullyConstrained = true
  MapMode = 5
  Placement = pos=(0,0,0) rot=(1,0,0;1.5708rad)
  Support = -> [XZ_Plane013]
  expr: Constraints[1] = <<Properties>>.Handle_OD - 1
  sketch-geometry (2):
    g0: Circle CenterX=0 CenterY=0 CenterZ=0 NormalX=0 NormalY=0 NormalZ=1 AngleXU=0 Radius=10.25
    g1: Circle CenterX=0 CenterY=0 CenterZ=0 NormalX=0 NormalY=0 NormalZ=1 AngleXU=0 Radius=4
  constraints (4):
    c: Coincident(g0,g-1)
    c: Diameter(g0) = 20.5
    c: Coincident(g1,g0)
    c: Diameter(g1) = 8
FEATURE [PartDesign::Pad] Pad015
  Direction = (0,-1,-2e-16)
  Length = 10
  Length2 = 10
  Placement = pos=(0,0,0) rot=(1,0,0;1.5708rad)
  Profile = -> Sketch026
  ReferenceAxis = -> Sketch026 [N_Axis]
  Type = 0
FEATURE [PartDesign::Draft] Draft
  Angle = 2
  Base = -> Pad015 [Face1]
  BaseFeature = -> Pad015
  NeutralPlane = -> Pad015 [Face3]
  Placement = pos=(0,0,0) rot=(1,0,0;1.5708rad)
  SupportTransform = false
FEATURE [PartDesign::Body] Body013  label="WirePlug"
  Group = -> [Sketch026,Pad015,Draft]
  Origin = -> Origin013
  Placement = pos=(0,-190,0) rot=(0,0,1;0rad)
  Tip = -> Draft
COMPONENT P12 — recipe-attached ("Body_CutLink", modeled in this document).
Construction recipe (the document's own serialized feature program — sketch geometry with constraints, then the solid features built on it; lengths are millimeters unless a unit is written):

FEATURE [Sketcher::SketchObject] Sketch  label="base"
  FullyConstrained = true
  MapMode = 5
  Support = -> [XY_Plane001]
  expr: Constraints[1] = <<Properties>>.Head_ID
  sketch-geometry (1):
    g0: Circle CenterX=0 CenterY=0 CenterZ=0 NormalX=0 NormalY=0 NormalZ=1 AngleXU=0 Radius=25.7
  constraints (2):
    c: Coincident(g0,g-1)
    c: Diameter(g0) = 51.4
FEATURE [PartDesign::Pad] Pad  label="Base"
  Direction = (0,0,1)
  Length = 35
  Length2 = 35
  Profile = -> Sketch
  ReferenceAxis = -> Sketch [N_Axis]
  Type = 4
  expr: Length = <<Properties>>.Insert_Len / 2
  expr: Length2 = <<Properties>>.Insert_Len / 2
FEATURE [Sketcher::SketchObject] Sketch001  label="sensor_wire_slot"
  FullyConstrained = true
  MapMode = 5
  Support = -> [XY_Plane001]
  expr: Constraints[11] = <<Properties>>.Sensor_Wire_Track_Width
  expr: Constraints[1] = Sketch.Constraints[1]
  sketch-geometry (7):
    g0: Circle CenterX=0 CenterY=0 CenterZ=0 NormalX=0 NormalY=0 NormalZ=1 AngleXU=0 Radius=25.7
    g1: LineSegment StartX=-4 StartY=-25.3868 StartZ=0 EndX=-4 EndY=-14.4568 EndZ=0
    g2: LineSegment StartX=-4 StartY=-14.4568 StartZ=0 EndX=4 EndY=-14.4568 EndZ=0
    g3: LineSegment StartX=4 StartY=-14.4568 StartZ=0 EndX=4 EndY=-25.3868 EndZ=0
    g4: ArcOfCircle CenterX=0 CenterY=0 CenterZ=0 NormalX=0 NormalY=0 NormalZ=1 AngleXU=0 Radius=25.7 StartAngle=4.55611 EndAngle=4.86867
    g5: GeomPoint X=0 Y=-14.4568 Z=0
    g6: Circle CenterX=0 CenterY=0 CenterZ=0 NormalX=0 NormalY=0 NormalZ=1 AngleXU=0 Radius=15
  constraints (17):
    c: Coincident(g0,g-1)
    c: Diameter(g0) = 51.4
    c: Vertical(g1)
    c: Coincident(g2,g1)
    c: Horizontal(g2)
    c: Coincident(g3,g2)
    c: Vertical(g3)
    c: Coincident(g4,g0)
    c: Coincident(g4,g1)
    c: Coincident(g4,g3)
    c: PointOnObject(g3,g0)
    c: DistanceX(g2,g2) = 8
    c: Symmetric(g2,g2,g5)
    c: PointOnObject(g5,g-2)
    c: Coincident(g6,g4)
    c: Diameter(g6) = 30
    c: PointOnObject(g2,g6)
FEATURE [PartDesign::Pocket] Pocket  label="Sensor_Wire_Slot"
  BaseFeature = -> Pad
  Direction = (0,0,-1)
  Length = 35
  Length2 = 35
  Profile = -> Sketch001
  ReferenceAxis = -> Sketch001 [N_Axis]
  Type = 4
  expr: Length = <<Properties>>.Insert_Len / 2
  expr: Length2 = <<Properties>>.Insert_Len / 2
FEATURE [Sketcher::SketchObject] Sketch002  label="handle_hole"
  FullyConstrained = true
  MapMode = 5
  Placement = pos=(0,0,0) rot=(1,0,0;1.5708rad)
  Support = -> [XZ_Plane001]
  expr: Constraints[1] = <<Properties>>.Handle_OD + <<Properties>>.Clearance * 2
  sketch-geometry (1):
    g0: Circle CenterX=0 CenterY=0 CenterZ=0 NormalX=0 NormalY=0 NormalZ=1 AngleXU=0 Radius=10.95
  constraints (2):
    c: Coincident(g0,g-1)
    c: Diameter(g0) = 21.9
FEATURE [PartDesign::Pocket] Pocket001  label="Handle_hole"
  BaseFeature = -> Pocket
  Direction = (0,1,2e-16)
  Length = 25.7
  Length2 = 25.7
  Profile = -> Sketch002
  ReferenceAxis = -> Sketch002 [N_Axis]
  Type = 4
  expr: Length = <<Properties>>.Head_ID / 2
  expr: Length2 = <<Properties>>.Head_ID / 2
FEATURE [Sketcher::SketchObject] Sketch004  label="top_sensor_hole"
  FullyConstrained = true
  MapMode = 5
  Placement = pos=(0,0,0) rot=(0.57735,0.57735,0.57735;2.0944rad)
  Support = -> [YZ_Plane001]
  expr: Constraints[20] = <<Properties>>.Head_ID
  expr: Constraints[7] = <<Properties>>.Sensor_Diameter + 4
  sketch-geometry (9):
    g0: LineSegment StartX=-25.7 StartY=-17 StartZ=0 EndX=-25.7 EndY=17 EndZ=0
    g1: LineSegment StartX=25.7 StartY=17 StartZ=0 EndX=25.7 EndY=-17 EndZ=0
    g2: LineSegment StartX=25.7 StartY=-17 StartZ=0 EndX=-25.7 EndY=-17 EndZ=0
    g3: GeomPoint X=0 Y=0 Z=0
    g4: LineSegment StartX=10.5 StartY=17 StartZ=0 EndX=25.7 EndY=17 EndZ=0
    g5: LineSegment StartX=25.7 StartY=17 StartZ=0 EndX=25.7 EndY=-17 EndZ=0
    g6: LineSegment StartX=25.7 StartY=-17 StartZ=0 EndX=10.5 EndY=-17 EndZ=0
    g7: LineSegment StartX=10.5 StartY=-17 StartZ=0 EndX=10.5 EndY=17 EndZ=0
    g8: LineSegment StartX=-25.7 StartY=17 StartZ=0 EndX=25.7 EndY=17 EndZ=0
  constraints (23):
    c: Coincident(g1,g2)
    c: Coincident(g2,g0)
    c: Horizontal(g2)
    c: Vertical(g0)
    c: Vertical(g1)
    c: Symmetric(g1,g0,g3)
    c: Coincident(g3,g-1)
    c: DistanceY(g1,g1) = 34
    c: Coincident(g4,g5)
    c: Coincident(g5,g6)
    c: Coincident(g6,g7)
    c: Horizontal(g4)
    c: Horizontal(g6)
    c: Vertical(g5)
    c: Vertical(g7)
    c: PointOnObject(g5,g2)
    c: Coincident(g7,g4)
    c: Coincident(g8,g0)
    c: Coincident(g8,g1)
    c: Horizontal(g8)
    c: DistanceX(g8,g8) = 51.4
    c: Coincident(g4,g1)
    c: DistanceX(g3,g4) = 10.5
FEATURE [PartDesign::Pocket] Pocket002  label="Top_Sensor_Hole"
  BaseFeature = -> Pocket001
  Direction = (-1,2e-16,-3e-16)
  Length = 17
  Length2 = 17
  Profile = -> Sketch004
  ReferenceAxis = -> Sketch004 [N_Axis]
  Type = 4
  expr: Length = <<Properties>>.Sensor_Diameter / 2 + 2
  expr: Length2 = <<Properties>>.Sensor_Diameter / 2 + 2
FEATURE [PartDesign::Chamfer] Chamfer
  Angle = 70
  Base = -> Pocket002 [Edge30,Edge32]
  BaseFeature = -> Pocket002
  ChamferType = 2
  FlipDirection = false
  Size = 8
  Size2 = 1
  SupportTransform = false
  UseAllEdges = false
FEATURE [Sketcher::SketchObject] Sketch003  label="spring_plate_slot"
  FullyConstrained = true
  MapMode = 5
  Support = -> [XY_Plane001]
  expr: Constraints[1] = Sketch.Constraints[1]
  expr: Constraints[3] = <<Properties>>.Sensor_Diameter + <<Properties>>.Clearance * 2
  expr: Constraints[7] = <<Properties>>.Spring_Plate_Len
  sketch-geometry (15):
    g0: Circle CenterX=0 CenterY=0 CenterZ=0 NormalX=0 NormalY=0 NormalZ=1 AngleXU=0 Radius=25.7
    g1: LineSegment StartX=-15.2 StartY=15.4669 StartZ=0 EndX=15.2 EndY=15.4669 EndZ=0
    g2: GeomPoint X=0 Y=15.4669 Z=0
    g3: LineSegment StartX=-23 StartY=11.4669 StartZ=0 EndX=23 EndY=11.4669 EndZ=0
    g4: GeomPoint X=0 Y=11.4669 Z=0
    g5: LineSegment StartX=-15.2 StartY=15.4669 StartZ=0 EndX=-21 EndY=11.4669 EndZ=0
    g6: LineSegment StartX=15.2 StartY=15.4669 StartZ=0 EndX=21 EndY=11.4669 EndZ=0
    g7: LineSegment StartX=21 StartY=11.4669 StartZ=0 EndX=23 EndY=11.4669 EndZ=0
    g8: LineSegment StartX=-21 StartY=11.4669 StartZ=0 EndX=-23 EndY=11.4669 EndZ=0
    g9: ArcOfCircle CenterX=0 CenterY=0 CenterZ=0 NormalX=0 NormalY=0 NormalZ=1 AngleXU=0 Radius=25.7 StartAngle=2.6791 EndAngle=2.80587
    g10: ArcOfCircle CenterX=0 CenterY=0 CenterZ=0 NormalX=0 NormalY=0 NormalZ=1 AngleXU=0 Radius=25.7 StartAngle=0.335723 EndAngle=0.462496
    g11: LineSegment StartX=-11 StartY=10.5 StartZ=0 EndX=-24.2652 EndY=8.46691 EndZ=0
    g12: LineSegment StartX=11 StartY=10.5 StartZ=0 EndX=24.2652 EndY=8.46691 EndZ=0
    g13: LineSegment StartX=11 StartY=10.5 StartZ=0 EndX=-11 EndY=10.5 EndZ=0
    g14: GeomPoint X=0 Y=10.5 Z=0
  constraints (39):
    c: Coincident(g0,g-1)
    c: Diameter(g0) = 51.4
    c: Horizontal(g1)
    c: DistanceX(g1,g1) = 30.4
    c: Symmetric(g1,g1,g2)
    c: PointOnObject(g2,g-2)
    c: Horizontal(g3)
    c: DistanceX(g3,g3) = 46
    c: Symmetric(g3,g3,g4)
    c: PointOnObject(g4,g-2)
    c: Coincident(g5,g1)
    c: PointOnObject(g5,g3)
    c: Coincident(g6,g1)
    c: PointOnObject(g6,g3)
    c: Coincident(g7,g6)
    c: PointOnObject(g7,g0)
    c: Horizontal(g7)
    c: Coincident(g8,g5)
    c: PointOnObject(g8,g0)
    c: Horizontal(g8)
    c: Equal(g8,g7)
    c: PointOnObject(g3,g0)
    c: DistanceY(g6,g1) = 4
    c: DistanceX(g6,g7) = 2
    c: Coincident(g9,g0)
    c: Coincident(g9,g8)
    c: Coincident(g10,g9)
    c: Coincident(g10,g7)
    c: Coincident(g13,g12)
    c: Coincident(g13,g11)
    c: Horizontal(g13)
    c: Coincident(g10,g12)
    c: Coincident(g9,g11)
    c: DistanceX(g12,g6) = 10
    c: Equal(g12,g11)
    c: DistanceY(g10,g7) = 3
    c: Symmetric(g13,g13,g14)
    c: PointOnObject(g14,g-2)
    c: DistanceY(g9,g14) = 10.5
FEATURE [PartDesign::Pocket] Pocket003  label="Spring_Plate_Slot"
  BaseFeature = -> Chamfer
  Direction = (0,0,-1)
  Length = 10
  Length2 = 10
  Profile = -> Sketch003
  ReferenceAxis = -> Sketch003 [N_Axis]
  Type = 4
FEATURE [PartDesign::Chamfer] Chamfer001
  Angle = 45
  Base = -> Pocket003 [Edge43,Edge46,Edge45,Edge47,Edge44,Edge42]
  BaseFeature = -> Pocket003
  ChamferType = 0
  FlipDirection = false
  Size = 0.5
  Size2 = 1
  SupportTransform = false
  UseAllEdges = false
FEATURE [Sketcher::SketchObject] Sketch008
  FullyConstrained = true
  MapMode = 5
  Placement = pos=(0,0,0) rot=(0.57735,0.57735,0.57735;2.0944rad)
  Support = -> [YZ_Plane001]
  expr: Constraints[16] = <<Properties>>.Sensor_Diameter + 2
  sketch-geometry (14):
    g0: LineSegment StartX=15.5 StartY=21 StartZ=0 EndX=15.5 EndY=-21 EndZ=0
    g1: LineSegment StartX=15.5 StartY=-21 StartZ=0 EndX=-19.02 EndY=-21 EndZ=0
    g2: LineSegment StartX=-19.02 StartY=-21 StartZ=0 EndX=-19.02 EndY=-16 EndZ=0
    g3: LineSegment StartX=-19.02 StartY=-16 StartZ=0 EndX=10.5 EndY=-16 EndZ=0
    g4: LineSegment StartX=10.5 StartY=-16 StartZ=0 EndX=10.5 EndY=16 EndZ=0
    g5: LineSegment StartX=10.5 StartY=16 StartZ=0 EndX=-19.02 EndY=16 EndZ=0
    g6: LineSegment StartX=-19.02 StartY=16 StartZ=0 EndX=-19.02 EndY=21 EndZ=0
    g7: LineSegment StartX=-19.02 StartY=21 StartZ=0 EndX=15.5 EndY=21 EndZ=0
    g8: GeomPoint X=10.5 Y=0 Z=0
    g9: GeomPoint X=15.5 Y=0 Z=0
    g10: GeomPoint X=15.5 Y=21 Z=0
    g11: GeomPoint X=15.5 Y=-21 Z=0
    g12: GeomPoint X=10.5 Y=16 Z=0
    g13: GeomPoint X=10.5 Y=-16 Z=0
  constraints (30):
    c: Vertical(g0)
    c: Horizontal(g1)
    c: Coincident(g2,g1)
    c: Vertical(g2)
    c: Coincident(g3,g2)
    c: Horizontal(g3)
    c: Vertical(g4)
    c: Horizontal(g5)
    c: Coincident(g6,g5)
    c: Vertical(g6)
    c: Coincident(g7,g6)
    c: Horizontal(g7)
    c: Symmetric(g10,g11,g9)
    c: Symmetric(g13,g12,g8)
    c: PointOnObject(g8,g-1)
    c: PointOnObject(g9,g-1)
    c: DistanceY(g13,g12) = 32
    c: DistanceY(g6,g6) = 5
    c: DistanceX(g8,g9) = 5
    c: DistanceX(g-1,g8) = 10.5
    c: DistanceX(g7,g10) = 34.52
    c: Coincident(g0,g10)
    c: Coincident(g7,g0)
    c: Coincident(g4,g12)
    c: Coincident(g5,g4)
    c: Coincident(g0,g11)
    c: Coincident(g4,g13)
    c: Coincident(g3,g4)
    c: Coincident(g1,g0)
    c: Equal(g3,g5)
FEATURE [PartDesign::Pocket] Pocket006
  BaseFeature = -> Chamfer001
  Direction = (-1,2e-16,-3e-16)
  Length = 4
  Length2 = 4
  Profile = -> Sketch008
  ReferenceAxis = -> Sketch008 [N_Axis]
  Type = 4
  expr: Length = <<Properties>>.Sensor_Wire_Track_Width / 2
  expr: Length2 = <<Properties>>.Sensor_Wire_Track_Width / 2
FEATURE [PartDesign::Chamfer] Chamfer003
  Angle = 65
  Base = -> Pocket006 [Edge148,Edge154]
  BaseFeature = -> Pocket006
  ChamferType = 2
  FlipDirection = false
  Size = 3
  Size2 = 1
  SupportTransform = false
  UseAllEdges = false
FEATURE [PartDesign::Chamfer] Chamfer004
  Angle = 45
  Base = -> Chamfer003 [Edge167,Edge85,Edge52,Edge56]
  BaseFeature = -> Chamfer003
  ChamferType = 0
  FlipDirection = false
  Size = 2
  Size2 = 1
  SupportTransform = false
  UseAllEdges = false
FEATURE [PartDesign::Chamfer] Chamfer005
  Angle = 45
  Base = -> Chamfer004 [Edge169,Edge38]
  BaseFeature = -> Chamfer004
  ChamferType = 1
  FlipDirection = false
  Size = 4
  Size2 = 3.999
  SupportTransform = false
  UseAllEdges = false
FEATURE [PartDesign::AdditiveCone] Cone
  Angle = 360
  AttacherType = Attacher::AttachEngine3D
  BaseFeature = -> Chamfer005
  Height = 1.5
  MapMode = 5
  Placement = pos=(0,0,35) rot=(0,0,1;0rad)
  Radius1 = 12
  Radius2 = 6
  Support = -> [Chamfer005]
FEATURE [PartDesign::AdditiveCone] Cone001
  Angle = 360
  AttacherType = Attacher::AttachEngine3D
  BaseFeature = -> Cone
  Height = 1.5
  MapMode = 5
  Placement = pos=(0,0,-35) rot=(1,0,0;3.14159rad)
  Radius1 = 12
  Radius2 = 6
  Support = -> [Cone]
FEATURE [Sketcher::SketchObject] Sketch022
  ExternalGeometry = -> [Cone001]
  FullyConstrained = true
  MapMode = 5
  Placement = pos=(2.3e-15,10.5,-35) rot=(-1,0,0;1.5708rad)
  Support = -> [Cone001]
  expr: Constraints[11] = <<Properties>>.Handle_OD + 2
  sketch-geometry (5):
    g0: LineSegment StartX=-11.75 StartY=-46.75 StartZ=0 EndX=-11.75 EndY=-23.25 EndZ=0
    g1: LineSegment StartX=-11.75 StartY=-23.25 StartZ=0 EndX=11.75 EndY=-23.25 EndZ=0
    g2: LineSegment StartX=11.75 StartY=-23.25 StartZ=0 EndX=11.75 EndY=-46.75 EndZ=0
    g3: LineSegment StartX=11.75 StartY=-46.75 StartZ=0 EndX=-11.75 EndY=-46.75 EndZ=0
    g4: GeomPoint X=-2.3e-15 Y=-35 Z=0
  constraints (12):
    c: Coincident(g0,g1)
    c: Coincident(g1,g2)
    c: Coincident(g2,g3)
    c: Coincident(g3,g0)
    c: Horizontal(g1)
    c: Horizontal(g3)
    c: Vertical(g0)
    c: Vertical(g2)
    c: Symmetric(g1,g0,g4)
    c: Coincident(g4,g-3)
    c: Equal(g2,g1)
    c: DistanceX(g1,g1) = 23.5
FEATURE [PartDesign::Pocket] Pocket010
  BaseFeature = -> Cone001
  Direction = (-2e-16,-1,2e-16)
  Length = 8
  Length2 = 5
  Placement = pos=(0,0,-35) rot=(1,0,0;3.14159rad)
  Profile = -> Sketch022
  ReferenceAxis = -> Sketch022 [N_Axis]
  Type = 0
FEATURE [Sketcher::SketchObject] Sketch024
  ExternalGeometry = -> [Cone001]
  FullyConstrained = true
  MapMode = 5
  Placement = pos=(6e-16,2.5,-35) rot=(-1,0,0;1.5708rad)
  Support = -> [Pocket010]
  expr: Constraints[11] = Sketch022.Constraints[11]
  expr: Constraints[54] = Sketch019.Constraints[43]
  expr: Constraints[55] = Sketch019.Constraints[44]
  sketch-geometry (34):
    g0: LineSegment StartX=-11.75 StartY=-46.75 StartZ=0 EndX=-11.75 EndY=-23.25 EndZ=0
    g1: LineSegment StartX=-11.75 StartY=-23.25 StartZ=0 EndX=11.75 EndY=-23.25 EndZ=0
    g2: LineSegment StartX=11.75 StartY=-23.25 StartZ=0 EndX=11.75 EndY=-46.75 EndZ=0
    g3: LineSegment StartX=11.75 StartY=-46.75 StartZ=0 EndX=-11.75 EndY=-46.75 EndZ=0
    g4: GeomPoint X=-2.4e-15 Y=-35 Z=0
    g5: LineSegment StartX=12 StartY=-37 StartZ=0 EndX=12 EndY=-33 EndZ=0
    g6: LineSegment StartX=12 StartY=-33 StartZ=0 EndX=2 EndY=-33 EndZ=0
    g7: LineSegment StartX=2 StartY=-33 StartZ=0 EndX=2 EndY=-23 EndZ=0
    g8: LineSegment StartX=2 StartY=-23 StartZ=0 EndX=-2 EndY=-23 EndZ=0
    g9: LineSegment StartX=-2 StartY=-23 StartZ=0 EndX=-2 EndY=-33 EndZ=0
    g10: LineSegment StartX=-2 StartY=-33 StartZ=0 EndX=-12 EndY=-33 EndZ=0
    g11: LineSegment StartX=-12 StartY=-33 StartZ=0 EndX=-12 EndY=-37 EndZ=0
    g12: LineSegment StartX=-12 StartY=-37 StartZ=0 EndX=-2 EndY=-37 EndZ=0
    g13: LineSegment StartX=-2 StartY=-37 StartZ=0 EndX=-2 EndY=-47 EndZ=0
    g14: LineSegment StartX=-2 StartY=-47 StartZ=0 EndX=2 EndY=-47 EndZ=0
    g15: LineSegment StartX=2 StartY=-47 StartZ=0 EndX=2 EndY=-37 EndZ=0
    g16: LineSegment StartX=2 StartY=-37 StartZ=0 EndX=12 EndY=-37 EndZ=0
    g17: LineSegment StartX=-2 StartY=-37 StartZ=0 EndX=-2 EndY=-33 EndZ=0
    g18: LineSegment StartX=-2 StartY=-33 StartZ=0 EndX=2 EndY=-33 EndZ=0
    g19: LineSegment StartX=2 StartY=-33 StartZ=0 EndX=2 EndY=-37 EndZ=0
    g20: LineSegment StartX=2 StartY=-37 StartZ=0 EndX=-2 EndY=-37 EndZ=0
    g21: GeomPoint X=0 Y=0 Z=0
    g22: LineSegment StartX=-2 StartY=-23.25 StartZ=0 EndX=2 EndY=-23.25 EndZ=0
    g23: LineSegment StartX=2 StartY=-23.25 StartZ=0 EndX=2 EndY=-33 EndZ=0
    g24: LineSegment StartX=2 StartY=-33 StartZ=0 EndX=11.75 EndY=-33 EndZ=0
    g25: LineSegment StartX=11.75 StartY=-33 StartZ=0 EndX=11.75 EndY=-37 EndZ=0
    g26: LineSegment StartX=11.75 StartY=-37 StartZ=0 EndX=2 EndY=-37 EndZ=0
    g27: LineSegment StartX=2 StartY=-37 StartZ=0 EndX=2 EndY=-46.75 EndZ=0
    g28: LineSegment StartX=2 StartY=-46.75 StartZ=0 EndX=-2 EndY=-46.75 EndZ=0
    g29: LineSegment StartX=-2 StartY=-46.75 StartZ=0 EndX=-2 EndY=-37 EndZ=0
    g30: LineSegment StartX=-2 StartY=-37 StartZ=0 EndX=-11.75 EndY=-37 EndZ=0
    g31: LineSegment StartX=-11.75 StartY=-37 StartZ=0 EndX=-11.75 EndY=-33 EndZ=0
    g32: LineSegment StartX=-11.75 StartY=-33 StartZ=0 EndX=-2 EndY=-33 EndZ=0
    g33: LineSegment StartX=-2 StartY=-33 StartZ=0 EndX=-2 EndY=-23.25 EndZ=0
  constraints (90):
    c: Coincident(g0,g1)
    c: Coincident(g1,g2)
    c: Coincident(g2,g3)
    c: Coincident(g3,g0)
    c: Horizontal(g1)
    c: Horizontal(g3)
    c: Vertical(g0)
    c: Vertical(g2)
    c: Symmetric(g1,g0,g4)
    c: Coincident(g4,g-3)
    c: Equal(g2,g1)
    c: DistanceX(g1,g1) = 23.5
    c: Vertical(g5)
    c: Coincident(g6,g5)
    c: Horizontal(g6)
    c: Coincident(g7,g6)
    c: Vertical(g7)
    c: Coincident(g8,g7)
    c: Horizontal(g8)
    c: Coincident(g9,g8)
    c: Vertical(g9)
    c: Coincident(g10,g9)
    c: Horizontal(g10)
    c: Coincident(g11,g10)
    c: Vertical(g11)
    c: Horizontal(g12)
    c: Coincident(g13,g12)
    c: Vertical(g13)
    c: Horizontal(g14)
    c: Coincident(g15,g14)
    c: Vertical(g15)
    c: Coincident(g16,g15)
    c: Coincident(g16,g5)
    c: Horizontal(g16)
    c: Equal(g5,g8)
    c: Equal(g8,g11)
    c: Equal(g11,g14)
    c: Coincident(g11,g12)
    c: Coincident(g14,g13)
    c: Equal(g16,g12)
    c: Equal(g16,g6)
    c: Equal(g7,g9)
    c: Equal(g10,g15)
    c: Coincident(g17,g18)
    c: Coincident(g18,g19)
    c: Coincident(g19,g20)
    c: Coincident(g20,g17)
    c: Horizontal(g18)
    c: Horizontal(g20)
    c: Vertical(g17)
    c: Vertical(g19)
    c: Coincident(g21,g-1)
    c: Coincident(g18,g6)
    c: Coincident(g12,g17)
    c: DistanceX(g18,g18) = 4
    c: DistanceY(g7,g7) = 10
    c: Equal(g15,g7)
    c: Symmetric(g6,g12,g4)
    c: PointOnObject(g22,g9)
    c: PointOnObject(g22,g1)
    c: Horizontal(g22)
    c: PointOnObject(g22,g7)
    c: Coincident(g23,g22)
    c: Coincident(g23,g6)
    c: Coincident(g24,g23)
    c: PointOnObject(g24,g2)
    c: Horizontal(g24)
    c: Coincident(g25,g24)
    c: PointOnObject(g25,g16)
    c: Vertical(g25)
    c: Coincident(g26,g25)
    c: Coincident(g26,g15)
    c: Coincident(g27,g26)
    c: PointOnObject(g27,g3)
    c: Vertical(g27)
    c: Coincident(g28,g27)
    c: PointOnObject(g28,g13)
    c: Horizontal(g28)
    c: Coincident(g29,g28)
    c: Coincident(g29,g12)
    c: Coincident(g30,g29)
    c: PointOnObject(g30,g0)
    c: Horizontal(g30)
    c: Coincident(g31,g30)
    c: PointOnObject(g31,g10)
    c: Vertical(g31)
    c: Coincident(g32,g31)
    c: Coincident(g32,g9)
    c: Coincident(g33,g32)
    c: Coincident(g33,g22)
FEATURE [PartDesign::Pocket] Pocket011
  BaseFeature = -> Pocket010
  Direction = (-2e-16,-1,2e-16)
  Length = 3
  Length2 = 5
  Placement = pos=(0,0,-35) rot=(1,0,0;3.14159rad)
  Profile = -> Sketch024
  ReferenceAxis = -> Sketch024 [N_Axis]
  Type = 0
FEATURE [PartDesign::Body] Body  label="HeadInstert"
  Group = -> [Sketch,Pad,Sketch001,Pocket,Sketch002,Pocket001,Sketch004,Pocket002,Chamfer,Sketch003,Pocket003,Chamfer001,Sketch008,Pocket006,Chamfer003,Chamfer004,Chamfer005,Cone,Cone001,Sketch022,Pocket010,Sketch024,Pocket011]
  Origin = -> Origin001
  Tip = -> Pocket011
COMPONENT P13 — recipe-attached ("Part", modeled in this document).
Construction recipe (the document's own serialized feature program — sketch geometry with constraints, then the solid features built on it; lengths are millimeters unless a unit is written):

FEATURE [Sketcher::SketchObject] Sketch  label="base"
  FullyConstrained = true
  MapMode = 5
  Support = -> [XY_Plane001]
  expr: Constraints[1] = <<Properties>>.Head_ID
  sketch-geometry (1):
    g0: Circle CenterX=0 CenterY=0 CenterZ=0 NormalX=0 NormalY=0 NormalZ=1 AngleXU=0 Radius=25.7
  constraints (2):
    c: Coincident(g0,g-1)
    c: Diameter(g0) = 51.4
FEATURE [PartDesign::Pad] Pad  label="Base"
  Direction = (0,0,1)
  Length = 35
  Length2 = 35
  Profile = -> Sketch
  ReferenceAxis = -> Sketch [N_Axis]
  Type = 4
  expr: Length = <<Properties>>.Insert_Len / 2
  expr: Length2 = <<Properties>>.Insert_Len / 2
FEATURE [Sketcher::SketchObject] Sketch001  label="sensor_wire_slot"
  FullyConstrained = true
  MapMode = 5
  Support = -> [XY_Plane001]
  expr: Constraints[11] = <<Properties>>.Sensor_Wire_Track_Width
  expr: Constraints[1] = Sketch.Constraints[1]
  sketch-geometry (7):
    g0: Circle CenterX=0 CenterY=0 CenterZ=0 NormalX=0 NormalY=0 NormalZ=1 AngleXU=0 Radius=25.7
    g1: LineSegment StartX=-4 StartY=-25.3868 StartZ=0 EndX=-4 EndY=-14.4568 EndZ=0
    g2: LineSegment StartX=-4 StartY=-14.4568 StartZ=0 EndX=4 EndY=-14.4568 EndZ=0
    g3: LineSegment StartX=4 StartY=-14.4568 StartZ=0 EndX=4 EndY=-25.3868 EndZ=0
    g4: ArcOfCircle CenterX=0 CenterY=0 CenterZ=0 NormalX=0 NormalY=0 NormalZ=1 AngleXU=0 Radius=25.7 StartAngle=4.55611 EndAngle=4.86867
    g5: GeomPoint X=0 Y=-14.4568 Z=0
    g6: Circle CenterX=0 CenterY=0 CenterZ=0 NormalX=0 NormalY=0 NormalZ=1 AngleXU=0 Radius=15
  constraints (17):
    c: Coincident(g0,g-1)
    c: Diameter(g0) = 51.4
    c: Vertical(g1)
    c: Coincident(g2,g1)
    c: Horizontal(g2)
    c: Coincident(g3,g2)
    c: Vertical(g3)
    c: Coincident(g4,g0)
    c: Coincident(g4,g1)
    c: Coincident(g4,g3)
    c: PointOnObject(g3,g0)
    c: DistanceX(g2,g2) = 8
    c: Symmetric(g2,g2,g5)
    c: PointOnObject(g5,g-2)
    c: Coincident(g6,g4)
    c: Diameter(g6) = 30
    c: PointOnObject(g2,g6)
FEATURE [PartDesign::Pocket] Pocket  label="Sensor_Wire_Slot"
  BaseFeature = -> Pad
  Direction = (0,0,-1)
  Length = 35
  Length2 = 35
  Profile = -> Sketch001
  ReferenceAxis = -> Sketch001 [N_Axis]
  Type = 4
  expr: Length = <<Properties>>.Insert_Len / 2
  expr: Length2 = <<Properties>>.Insert_Len / 2
FEATURE [Sketcher::SketchObject] Sketch002  label="handle_hole"
  FullyConstrained = true
  MapMode = 5
  Placement = pos=(0,0,0) rot=(1,0,0;1.5708rad)
  Support = -> [XZ_Plane001]
  expr: Constraints[1] = <<Properties>>.Handle_OD + <<Properties>>.Clearance * 2
  sketch-geometry (1):
    g0: Circle CenterX=0 CenterY=0 CenterZ=0 NormalX=0 NormalY=0 NormalZ=1 AngleXU=0 Radius=10.95
  constraints (2):
    c: Coincident(g0,g-1)
    c: Diameter(g0) = 21.9
FEATURE [PartDesign::Pocket] Pocket001  label="Handle_hole"
  BaseFeature = -> Pocket
  Direction = (0,1,2e-16)
  Length = 25.7
  Length2 = 25.7
  Profile = -> Sketch002
  ReferenceAxis = -> Sketch002 [N_Axis]
  Type = 4
  expr: Length = <<Properties>>.Head_ID / 2
  expr: Length2 = <<Properties>>.Head_ID / 2
FEATURE [Sketcher::SketchObject] Sketch004  label="top_sensor_hole"
  FullyConstrained = true
  MapMode = 5
  Placement = pos=(0,0,0) rot=(0.57735,0.57735,0.57735;2.0944rad)
  Support = -> [YZ_Plane001]
  expr: Constraints[20] = <<Properties>>.Head_ID
  expr: Constraints[7] = <<Properties>>.Sensor_Diameter + 4
  sketch-geometry (9):
    g0: LineSegment StartX=-25.7 StartY=-17 StartZ=0 EndX=-25.7 EndY=17 EndZ=0
    g1: LineSegment StartX=25.7 StartY=17 StartZ=0 EndX=25.7 EndY=-17 EndZ=0
    g2: LineSegment StartX=25.7 StartY=-17 StartZ=0 EndX=-25.7 EndY=-17 EndZ=0
    g3: GeomPoint X=0 Y=0 Z=0
    g4: LineSegment StartX=10.5 StartY=17 StartZ=0 EndX=25.7 EndY=17 EndZ=0
    g5: LineSegment StartX=25.7 StartY=17 StartZ=0 EndX=25.7 EndY=-17 EndZ=0
    g6: LineSegment StartX=25.7 StartY=-17 StartZ=0 EndX=10.5 EndY=-17 EndZ=0
    g7: LineSegment StartX=10.5 StartY=-17 StartZ=0 EndX=10.5 EndY=17 EndZ=0
    g8: LineSegment StartX=-25.7 StartY=17 StartZ=0 EndX=25.7 EndY=17 EndZ=0
  constraints (23):
    c: Coincident(g1,g2)
    c: Coincident(g2,g0)
    c: Horizontal(g2)
    c: Vertical(g0)
    c: Vertical(g1)
    c: Symmetric(g1,g0,g3)
    c: Coincident(g3,g-1)
    c: DistanceY(g1,g1) = 34
    c: Coincident(g4,g5)
    c: Coincident(g5,g6)
    c: Coincident(g6,g7)
    c: Horizontal(g4)
    c: Horizontal(g6)
    c: Vertical(g5)
    c: Vertical(g7)
    c: PointOnObject(g5,g2)
    c: Coincident(g7,g4)
    c: Coincident(g8,g0)
    c: Coincident(g8,g1)
    c: Horizontal(g8)
    c: DistanceX(g8,g8) = 51.4
    c: Coincident(g4,g1)
    c: DistanceX(g3,g4) = 10.5
FEATURE [PartDesign::Pocket] Pocket002  label="Top_Sensor_Hole"
  BaseFeature = -> Pocket001
  Direction = (-1,2e-16,-3e-16)
  Length = 17
  Length2 = 17
  Profile = -> Sketch004
  ReferenceAxis = -> Sketch004 [N_Axis]
  Type = 4
  expr: Length = <<Properties>>.Sensor_Diameter / 2 + 2
  expr: Length2 = <<Properties>>.Sensor_Diameter / 2 + 2
FEATURE [PartDesign::Chamfer] Chamfer
  Angle = 70
  Base = -> Pocket002 [Edge30,Edge32]
  BaseFeature = -> Pocket002
  ChamferType = 2
  FlipDirection = false
  Size = 8
  Size2 = 1
  SupportTransform = false
  UseAllEdges = false
FEATURE [Sketcher::SketchObject] Sketch003  label="spring_plate_slot"
  FullyConstrained = true
  MapMode = 5
  Support = -> [XY_Plane001]
  expr: Constraints[1] = Sketch.Constraints[1]
  expr: Constraints[3] = <<Properties>>.Sensor_Diameter + <<Properties>>.Clearance * 2
  expr: Constraints[7] = <<Properties>>.Spring_Plate_Len
  sketch-geometry (15):
    g0: Circle CenterX=0 CenterY=0 CenterZ=0 NormalX=0 NormalY=0 NormalZ=1 AngleXU=0 Radius=25.7
    g1: LineSegment StartX=-15.2 StartY=15.4669 StartZ=0 EndX=15.2 EndY=15.4669 EndZ=0
    g2: GeomPoint X=0 Y=15.4669 Z=0
    g3: LineSegment StartX=-23 StartY=11.4669 StartZ=0 EndX=23 EndY=11.4669 EndZ=0
    g4: GeomPoint X=0 Y=11.4669 Z=0
    g5: LineSegment StartX=-15.2 StartY=15.4669 StartZ=0 EndX=-21 EndY=11.4669 EndZ=0
    g6: LineSegment StartX=15.2 StartY=15.4669 StartZ=0 EndX=21 EndY=11.4669 EndZ=0
    g7: LineSegment StartX=21 StartY=11.4669 StartZ=0 EndX=23 EndY=11.4669 EndZ=0
    g8: LineSegment StartX=-21 StartY=11.4669 StartZ=0 EndX=-23 EndY=11.4669 EndZ=0
    g9: ArcOfCircle CenterX=0 CenterY=0 CenterZ=0 NormalX=0 NormalY=0 NormalZ=1 AngleXU=0 Radius=25.7 StartAngle=2.6791 EndAngle=2.80587
    g10: ArcOfCircle CenterX=0 CenterY=0 CenterZ=0 NormalX=0 NormalY=0 NormalZ=1 AngleXU=0 Radius=25.7 StartAngle=0.335723 EndAngle=0.462496
    g11: LineSegment StartX=-11 StartY=10.5 StartZ=0 EndX=-24.2652 EndY=8.46691 EndZ=0
    g12: LineSegment StartX=11 StartY=10.5 StartZ=0 EndX=24.2652 EndY=8.46691 EndZ=0
    g13: LineSegment StartX=11 StartY=10.5 StartZ=0 EndX=-11 EndY=10.5 EndZ=0
    g14: GeomPoint X=0 Y=10.5 Z=0
  constraints (39):
    c: Coincident(g0,g-1)
    c: Diameter(g0) = 51.4
    c: Horizontal(g1)
    c: DistanceX(g1,g1) = 30.4
    c: Symmetric(g1,g1,g2)
    c: PointOnObject(g2,g-2)
    c: Horizontal(g3)
    c: DistanceX(g3,g3) = 46
    c: Symmetric(g3,g3,g4)
    c: PointOnObject(g4,g-2)
    c: Coincident(g5,g1)
    c: PointOnObject(g5,g3)
    c: Coincident(g6,g1)
    c: PointOnObject(g6,g3)
    c: Coincident(g7,g6)
    c: PointOnObject(g7,g0)
    c: Horizontal(g7)
    c: Coincident(g8,g5)
    c: PointOnObject(g8,g0)
    c: Horizontal(g8)
    c: Equal(g8,g7)
    c: PointOnObject(g3,g0)
    c: DistanceY(g6,g1) = 4
    c: DistanceX(g6,g7) = 2
    c: Coincident(g9,g0)
    c: Coincident(g9,g8)
    c: Coincident(g10,g9)
    c: Coincident(g10,g7)
    c: Coincident(g13,g12)
    c: Coincident(g13,g11)
    c: Horizontal(g13)
    c: Coincident(g10,g12)
    c: Coincident(g9,g11)
    c: DistanceX(g12,g6) = 10
    c: Equal(g12,g11)
    c: DistanceY(g10,g7) = 3
    c: Symmetric(g13,g13,g14)
    c: PointOnObject(g14,g-2)
    c: DistanceY(g9,g14) = 10.5
FEATURE [PartDesign::Pocket] Pocket003  label="Spring_Plate_Slot"
  BaseFeature = -> Chamfer
  Direction = (0,0,-1)
  Length = 10
  Length2 = 10
  Profile = -> Sketch003
  ReferenceAxis = -> Sketch003 [N_Axis]
  Type = 4
FEATURE [PartDesign::Chamfer] Chamfer001
  Angle = 45
  Base = -> Pocket003 [Edge43,Edge46,Edge45,Edge47,Edge44,Edge42]
  BaseFeature = -> Pocket003
  ChamferType = 0
  FlipDirection = false
  Size = 0.5
  Size2 = 1
  SupportTransform = false
  UseAllEdges = false
FEATURE [Sketcher::SketchObject] Sketch005  label="top_sens_base"
  FullyConstrained = true
  MapMode = 5
  Support = -> [XY_Plane]
  expr: Constraints[18] = <<Properties>>.Clearance
  expr: Constraints[1] = <<Properties>>.Head_ID
  expr: Constraints[3] = 34 - <<Properties>>.Clearance * 2
  expr: Constraints[6] = 10.5 + <<Properties>>.Clearance
  sketch-geometry (8):
    g0: Circle CenterX=0 CenterY=0 CenterZ=0 NormalX=0 NormalY=0 NormalZ=1 AngleXU=0 Radius=25.7
    g1: LineSegment StartX=-16.8 StartY=10.7 StartZ=0 EndX=16.8 EndY=10.7 EndZ=0
    g2: GeomPoint X=0 Y=10.7 Z=0
    g3: LineSegment StartX=-16.8 StartY=10.7 StartZ=0 EndX=-16.8 EndY=19.1836 EndZ=0
    g4: LineSegment StartX=16.8 StartY=10.7 StartZ=0 EndX=16.8 EndY=19.1836 EndZ=0
    g5: GeomPoint X=0 Y=25.7 Z=0
    g6: ArcOfCircle CenterX=0 CenterY=0 CenterZ=0 NormalX=0 NormalY=0 NormalZ=1 AngleXU=0 Radius=25.5 StartAngle=0.851542 EndAngle=2.29005
    g7: GeomPoint X=0 Y=25.5 Z=0
  constraints (19):
    c: Coincident(g0,g-1)
    c: Diameter(g0) = 51.4
    c: Horizontal(g1)
    c: DistanceX(g1,g1) = 33.6
    c: Symmetric(g1,g1,g2)
    c: PointOnObject(g2,g-2)
    c: DistanceY(g0,g2) = 10.7
    c: Coincident(g3,g1)
    c: Vertical(g3)
    c: Vertical(g4)
    c: Coincident(g4,g1)
    c: PointOnObject(g5,g0)
    c: PointOnObject(g5,g-2)
    c: Coincident(g6,g0)
    c: Coincident(g6,g3)
    c: Coincident(g6,g4)
    c: PointOnObject(g7,g6)
    c: PointOnObject(g7,g-2)
    c: DistanceY(g7,g5) = 0.2
FEATURE [PartDesign::Pad] Pad001  label="Top_Base"
  Direction = (0,0,1)
  Length = 16.8
  Length2 = 16.8
  Profile = -> Sketch005
  ReferenceAxis = -> Sketch005 [N_Axis]
  Type = 4
  expr: Length = <<Properties>>.Sensor_Diameter / 2 + 2 - <<Properties>>.Clearance
  expr: Length2 = <<Properties>>.Sensor_Diameter / 2 + 2 - <<Properties>>.Clearance
FEATURE [Sketcher::SketchObject] Sketch006
  FullyConstrained = true
  MapMode = 5
  Support = -> [XY_Plane]
  expr: Constraints[1] = Sketch003.Constraints[1]
  expr: Constraints[22] = Sketch003.Constraints[22]
  expr: Constraints[23] = Sketch003.Constraints[23]
  expr: Constraints[33] = Sketch003.Constraints[33]
  expr: Constraints[35] = Sketch003.Constraints[35]
  expr: Constraints[38] = Sketch003.Constraints[38]
  expr: Constraints[3] = Sketch003.Constraints[3]
  expr: Constraints[7] = Sketch003.Constraints[7]
  sketch-geometry (15):
    g0: Circle CenterX=0 CenterY=0 CenterZ=0 NormalX=0 NormalY=0 NormalZ=1 AngleXU=0 Radius=25.7
    g1: LineSegment StartX=-15.2 StartY=15.4669 StartZ=0 EndX=15.2 EndY=15.4669 EndZ=0
    g2: GeomPoint X=0 Y=15.4669 Z=0
    g3: LineSegment StartX=-23 StartY=11.4669 StartZ=0 EndX=23 EndY=11.4669 EndZ=0
    g4: GeomPoint X=0 Y=11.4669 Z=0
    g5: LineSegment StartX=-15.2 StartY=15.4669 StartZ=0 EndX=-21 EndY=11.4669 EndZ=0
    g6: LineSegment StartX=15.2 StartY=15.4669 StartZ=0 EndX=21 EndY=11.4669 EndZ=0
    g7: LineSegment StartX=21 StartY=11.4669 StartZ=0 EndX=23 EndY=11.4669 EndZ=0
    g8: LineSegment StartX=-21 StartY=11.4669 StartZ=0 EndX=-23 EndY=11.4669 EndZ=0
    g9: ArcOfCircle CenterX=0 CenterY=0 CenterZ=0 NormalX=0 NormalY=0 NormalZ=1 AngleXU=0 Radius=25.7 StartAngle=2.6791 EndAngle=2.80587
    g10: ArcOfCircle CenterX=0 CenterY=0 CenterZ=0 NormalX=0 NormalY=0 NormalZ=1 AngleXU=0 Radius=25.7 StartAngle=0.335723 EndAngle=0.462496
    g11: LineSegment StartX=-11 StartY=10.5 StartZ=0 EndX=-24.2652 EndY=8.46691 EndZ=0
    g12: LineSegment StartX=11 StartY=10.5 StartZ=0 EndX=24.2652 EndY=8.46691 EndZ=0
    g13: LineSegment StartX=11 StartY=10.5 StartZ=0 EndX=-11 EndY=10.5 EndZ=0
    g14: GeomPoint X=0 Y=10.5 Z=0
  constraints (40):
    c: Coincident(g0,g-1)
    c: Diameter(g0) = 51.4
    c: Horizontal(g1)
    c: DistanceX(g1,g1) = 30.4
    c: Symmetric(g1,g1,g2)
    c: PointOnObject(g2,g-2)
    c: Horizontal(g3)
    c: DistanceX(g3,g3) = 46
    c: Symmetric(g3,g3,g4)
    c: PointOnObject(g4,g-2)
    c: Coincident(g5,g1)
    c: PointOnObject(g5,g3)
    c: Coincident(g6,g1)
    c: PointOnObject(g6,g3)
    c: Coincident(g7,g6)
    c: PointOnObject(g7,g0)
    c: Horizontal(g7)
    c: Coincident(g8,g5)
    c: PointOnObject(g8,g0)
    c: Horizontal(g8)
    c: Equal(g8,g7)
    c: PointOnObject(g3,g0)
    c: DistanceY(g6,g1) = 4
    c: DistanceX(g6,g7) = 2
    c: Coincident(g9,g0)
    c: Coincident(g9,g8)
    c: Coincident(g10,g9)
    c: Coincident(g10,g7)
    c: Coincident(g13,g12)
    c: Coincident(g13,g11)
    c: Horizontal(g13)
    c: Coincident(g10,g12)
    c: Coincident(g9,g11)
    c: DistanceX(g12,g6) = 10
    c: Equal(g12,g11)
    c: DistanceY(g10,g7) = 3
    c: Symmetric(g13,g13,g14)
    c: PointOnObject(g14,g-2)
    c: DistanceY(g9,g14) = 10.5
    c: DistanceY(g9,g2) = 15.4669
FEATURE [PartDesign::Pocket] Pocket004
  BaseFeature = -> Pad001
  Direction = (0,0,-1)
  Length = 9.5
  Length2 = 9.5
  Profile = -> Sketch006
  ReferenceAxis = -> Sketch006 [N_Axis]
  Type = 4
FEATURE [PartDesign::Chamfer] Chamfer002
  Angle = 45
  Base = -> Pocket004 [Edge22,Edge12]
  BaseFeature = -> Pocket004
  ChamferType = 0
  FlipDirection = false
  Size = 0.3
  Size2 = 1
  SupportTransform = false
  UseAllEdges = false
FEATURE [Sketcher::SketchObject] Sketch007
  FullyConstrained = true
  MapMode = 5
  Placement = pos=(0,0,0) rot=(1,0,0;1.5708rad)
  Support = -> [XZ_Plane]
  expr: Constraints[11] = <<Properties>>.Sensor_Wire_Track_Width
  expr: Constraints[1] = <<Properties>>.Sensor_Diameter + 1
  expr: Constraints[27] = <<Properties>>.Sensor_Wire_Track_Width
  sketch-geometry (11):
    g0: Circle CenterX=0 CenterY=0 CenterZ=0 NormalX=0 NormalY=0 NormalZ=1 AngleXU=0 Radius=15.5
    g1: LineSegment StartX=-4 StartY=14.975 StartZ=0 EndX=-4 EndY=27.305 EndZ=0
    g2: LineSegment StartX=-4 StartY=27.305 StartZ=0 EndX=4 EndY=27.305 EndZ=0
    g3: LineSegment StartX=4 StartY=27.305 StartZ=0 EndX=4 EndY=14.975 EndZ=0
    g4: GeomPoint X=0 Y=27.305 Z=0
    g5: LineSegment StartX=-4 StartY=-14.975 StartZ=0 EndX=-4 EndY=-27.305 EndZ=0
    g6: LineSegment StartX=-4 StartY=-27.305 StartZ=0 EndX=4 EndY=-27.305 EndZ=0
    g7: LineSegment StartX=4 StartY=-27.305 StartZ=0 EndX=4 EndY=-14.975 EndZ=0
    g8: GeomPoint X=0 Y=-27.305 Z=0
    g9: ArcOfCircle CenterX=0 CenterY=0 CenterZ=0 NormalX=0 NormalY=0 NormalZ=1 AngleXU=0 Radius=15.5 StartAngle=1.83181 EndAngle=4.45137
    g10: ArcOfCircle CenterX=0 CenterY=0 CenterZ=0 NormalX=0 NormalY=0 NormalZ=1 AngleXU=0 Radius=15.5 StartAngle=4.97341 EndAngle=7.59296
  constraints (28):
    c: Coincident(g0,g-1)
    c: Diameter(g0) = 31
    c: PointOnObject(g1,g0)
    c: Vertical(g1)
    c: Coincident(g2,g1)
    c: Horizontal(g2)
    c: Coincident(g3,g2)
    c: PointOnObject(g3,g0)
    c: Vertical(g3)
    c: Symmetric(g2,g2,g4)
    c: PointOnObject(g4,g-2)
    c: DistanceX(g2,g2) = 8
    c: DistanceY(g3,g3) = 12.33
    c: Vertical(g5)
    c: Coincident(g6,g5)
    c: Horizontal(g6)
    c: Coincident(g7,g6)
    c: Vertical(g7)
    c: Symmetric(g6,g6,g8)
    c: PointOnObject(g8,g-2)
    c: Equal(g7,g3)
    c: Coincident(g9,g0)
    c: Coincident(g9,g1)
    c: Coincident(g9,g5)
    c: Coincident(g10,g9)
    c: Coincident(g10,g3)
    c: Coincident(g10,g7)
    c: DistanceX(g6,g6) = 8
FEATURE [PartDesign::Pocket] Pocket005
  BaseFeature = -> Chamfer002
  Direction = (0,1,2e-16)
  Length = 0
  Length2 = 5
  Offset = 0.4
  Profile = -> Sketch007
  ReferenceAxis = -> Sketch007 [N_Axis]
  Type = 3
  UpToFace = -> Chamfer002 [Face11]
FEATURE [PartDesign::Body] Body001  label="TopSensor"
  Group = -> [Sketch005,Pad001,Sketch006,Pocket004,Chamfer002,Sketch007,Pocket005]
  Origin = -> Origin
  Tip = -> Pocket005
FEATURE [Sketcher::SketchObject] Sketch008
  FullyConstrained = true
  MapMode = 5
  Placement = pos=(0,0,0) rot=(0.57735,0.57735,0.57735;2.0944rad)
  Support = -> [YZ_Plane001]
  expr: Constraints[16] = <<Properties>>.Sensor_Diameter + 2
  sketch-geometry (14):
    g0: LineSegment StartX=15.5 StartY=21 StartZ=0 EndX=15.5 EndY=-21 EndZ=0
    g1: LineSegment StartX=15.5 StartY=-21 StartZ=0 EndX=-19.02 EndY=-21 EndZ=0
    g2: LineSegment StartX=-19.02 StartY=-21 StartZ=0 EndX=-19.02 EndY=-16 EndZ=0
    g3: LineSegment StartX=-19.02 StartY=-16 StartZ=0 EndX=10.5 EndY=-16 EndZ=0
    g4: LineSegment StartX=10.5 StartY=-16 StartZ=0 EndX=10.5 EndY=16 EndZ=0
    g5: LineSegment StartX=10.5 StartY=16 StartZ=0 EndX=-19.02 EndY=16 EndZ=0
    g6: LineSegment StartX=-19.02 StartY=16 StartZ=0 EndX=-19.02 EndY=21 EndZ=0
    g7: LineSegment StartX=-19.02 StartY=21 StartZ=0 EndX=15.5 EndY=21 EndZ=0
    g8: GeomPoint X=10.5 Y=0 Z=0
    g9: GeomPoint X=15.5 Y=0 Z=0
    g10: GeomPoint X=15.5 Y=21 Z=0
    g11: GeomPoint X=15.5 Y=-21 Z=0
    g12: GeomPoint X=10.5 Y=16 Z=0
    g13: GeomPoint X=10.5 Y=-16 Z=0
  constraints (30):
    c: Vertical(g0)
    c: Horizontal(g1)
    c: Coincident(g2,g1)
    c: Vertical(g2)
    c: Coincident(g3,g2)
    c: Horizontal(g3)
    c: Vertical(g4)
    c: Horizontal(g5)
    c: Coincident(g6,g5)
    c: Vertical(g6)
    c: Coincident(g7,g6)
    c: Horizontal(g7)
    c: Symmetric(g10,g11,g9)
    c: Symmetric(g13,g12,g8)
    c: PointOnObject(g8,g-1)
    c: PointOnObject(g9,g-1)
    c: DistanceY(g13,g12) = 32
    c: DistanceY(g6,g6) = 5
    c: DistanceX(g8,g9) = 5
    c: DistanceX(g-1,g8) = 10.5
    c: DistanceX(g7,g10) = 34.52
    c: Coincident(g0,g10)
    c: Coincident(g7,g0)
    c: Coincident(g4,g12)
    c: Coincident(g5,g4)
    c: Coincident(g0,g11)
    c: Coincident(g4,g13)
    c: Coincident(g3,g4)
    c: Coincident(g1,g0)
    c: Equal(g3,g5)
FEATURE [PartDesign::Pocket] Pocket006
  BaseFeature = -> Chamfer001
  Direction = (-1,2e-16,-3e-16)
  Length = 4
  Length2 = 4
  Profile = -> Sketch008
  ReferenceAxis = -> Sketch008 [N_Axis]
  Type = 4
  expr: Length = <<Properties>>.Sensor_Wire_Track_Width / 2
  expr: Length2 = <<Properties>>.Sensor_Wire_Track_Width / 2
FEATURE [PartDesign::Chamfer] Chamfer003
  Angle = 65
  Base = -> Pocket006 [Edge148,Edge154]
  BaseFeature = -> Pocket006
  ChamferType = 2
  FlipDirection = false
  Size = 3
  Size2 = 1
  SupportTransform = false
  UseAllEdges = false
FEATURE [PartDesign::Chamfer] Chamfer004
  Angle = 45
  Base = -> Chamfer003 [Edge167,Edge85,Edge52,Edge56]
  BaseFeature = -> Chamfer003
  ChamferType = 0
  FlipDirection = false
  Size = 2
  Size2 = 1
  SupportTransform = false
  UseAllEdges = false
FEATURE [PartDesign::Chamfer] Chamfer005
  Angle = 45
  Base = -> Chamfer004 [Edge169,Edge38]
  BaseFeature = -> Chamfer004
  ChamferType = 1
  FlipDirection = false
  Size = 4
  Size2 = 3.999
  SupportTransform = false
  UseAllEdges = false
FEATURE [Sketcher::SketchObject] Sketch009
  FullyConstrained = true
  MapMode = 5
  Support = -> [XY_Plane002]
  sketch-geometry (2):
    g0: Circle CenterX=0 CenterY=0 CenterZ=0 NormalX=0 NormalY=0 NormalZ=1 AngleXU=0 Radius=26
    g1: Circle CenterX=0 CenterY=0 CenterZ=0 NormalX=0 NormalY=0 NormalZ=1 AngleXU=0 Radius=30
  constraints (4):
    c: Coincident(g0,g-1)
    c: Coincident(g1,g0)
    c: Diameter(g0) = 52
    c: Diameter(g1) = 60
FEATURE [PartDesign::Pad] Pad002
  Direction = (0,0,1)
  Length = 45
  Length2 = 45
  Profile = -> Sketch009
  ReferenceAxis = -> Sketch009 [N_Axis]
  Type = 4
FEATURE [Sketcher::SketchObject] Sketch010
  FullyConstrained = true
  MapMode = 5
  Placement = pos=(0,0,0) rot=(1,0,0;1.5708rad)
  Support = -> [XZ_Plane002]
  expr: Constraints[1] = <<Properties>>.Handle_OD
  sketch-geometry (1):
    g0: Circle CenterX=0 CenterY=0 CenterZ=0 NormalX=0 NormalY=0 NormalZ=1 AngleXU=0 Radius=10.75
  constraints (2):
    c: Coincident(g0,g-1)
    c: Diameter(g0) = 21.5
FEATURE [PartDesign::Pocket] Pocket007
  BaseFeature = -> Pad002
  Direction = (0,1,2e-16)
  Length = 5
  Length2 = 5
  Profile = -> Sketch010
  ReferenceAxis = -> Sketch010 [N_Axis]
  Reversed = true
  Type = 1
FEATURE [Sketcher::SketchObject] Sketch011
  FullyConstrained = true
  MapMode = 5
  Placement = pos=(0,0,0) rot=(1,0,0;1.5708rad)
  Support = -> [XZ_Plane003]
  expr: Constraints[3] = <<Properties>>.Handle_ID
  sketch-geometry (2):
    g0: Circle CenterX=0 CenterY=0 CenterZ=0 NormalX=0 NormalY=0 NormalZ=1 AngleXU=0 Radius=10.625
    g1: Circle CenterX=0 CenterY=0 CenterZ=0 NormalX=0 NormalY=0 NormalZ=1 AngleXU=0 Radius=10.25
  constraints (4):
    c: Coincident(g0,g-1)
    c: Diameter(g0) = 21.25
    c: Coincident(g1,g0)
    c: Diameter(g1) = 20.5
FEATURE [PartDesign::Pad] Pad003
  Direction = (0,-1,-2e-16)
  Length = 200
  Length2 = 10
  Placement = pos=(0,0,0) rot=(1,0,0;1.5708rad)
  Profile = -> Sketch011
  ReferenceAxis = -> Sketch011 [N_Axis]
  Type = 0
FEATURE [Sketcher::SketchObject] Sketch014
  FullyConstrained = true
  MapMode = 5
  Support = -> [XY_Plane005]
  sketch-geometry (5):
    g0: ArcOfCircle CenterX=0 CenterY=0 CenterZ=0 NormalX=0 NormalY=0 NormalZ=1 AngleXU=0 Radius=15 StartAngle=4.90695 EndAngle=10.801
    g1: LineSegment StartX=2.9 StartY=-14.717 StartZ=0 EndX=2.9 EndY=-20.717 EndZ=0
    g2: LineSegment StartX=2.9 StartY=-20.717 StartZ=0 EndX=-2.9 EndY=-20.717 EndZ=0
    g3: LineSegment StartX=-2.9 StartY=-20.717 StartZ=0 EndX=-2.9 EndY=-14.717 EndZ=0
    g4: LineSegment StartX=2.9 StartY=-14.717 StartZ=0 EndX=-2.9 EndY=-14.717 EndZ=0
  constraints (14):
    c: Coincident(g0,g-1)
    c: Radius(g0) = 15
    c: Coincident(g1,g0)
    c: Vertical(g1)
    c: Coincident(g2,g1)
    c: Horizontal(g2)
    c: Coincident(g3,g2)
    c: Coincident(g3,g0)
    c: Vertical(g3)
    c: DistanceX(g2,g2) = 5.8
    c: Coincident(g4,g0)
    c: Coincident(g4,g0)
    c: Horizontal(g4)
    c: DistanceY(g1,g1) = 6
FEATURE [PartDesign::Pad] Pad007
  Direction = (0,0,1)
  Length = 1
  Length2 = 10
  Profile = -> Sketch014
  ReferenceAxis = -> Sketch014 [N_Axis]
  Type = 0
FEATURE [PartDesign::Body] Body005  label="Sensor1"
  Group = -> [Sketch014,Pad007]
  Origin = -> Origin005
  Placement = pos=(0,0,37) rot=(0,0,1;0rad)
  Tip = -> Pad007
FEATURE [PartDesign::FeatureBase] Clone
  BaseFeature = -> Body005
FEATURE [PartDesign::Body] Body006  label="Sensor2"
  Group = -> [Clone]
  Origin = -> Origin006
  Placement = pos=(0,0,-37) rot=(0,1,0;3.14159rad)
  Tip = -> Clone
FEATURE [PartDesign::FeatureBase] Clone001
  BaseFeature = -> Body005
FEATURE [PartDesign::Body] Body007  label="Sensor3"
  Group = -> [Clone001]
  Origin = -> Origin007
  Placement = pos=(0,16,-4e-15) rot=(0,0.707107,-0.707107;3.14159rad)
  Tip = -> Clone001
FEATURE [PartDesign::AdditiveCone] Cone
  Angle = 360
  AttacherType = Attacher::AttachEngine3D
  BaseFeature = -> Chamfer005
  Height = 1.5
  MapMode = 5
  Placement = pos=(0,0,35) rot=(0,0,1;0rad)
  Radius1 = 12
  Radius2 = 6
  Support = -> [Chamfer005]
FEATURE [PartDesign::AdditiveCone] Cone001
  Angle = 360
  AttacherType = Attacher::AttachEngine3D
  BaseFeature = -> Cone
  Height = 1.5
  MapMode = 5
  Placement = pos=(0,0,-35) rot=(1,0,0;3.14159rad)
  Radius1 = 12
  Radius2 = 6
  Support = -> [Cone]
FEATURE [Sketcher::SketchObject] Sketch015
  FullyConstrained = true
  MapMode = 5
  Support = -> [XY_Plane008]
  sketch-geometry (1):
    g0: Circle CenterX=0 CenterY=0 CenterZ=0 NormalX=0 NormalY=0 NormalZ=1 AngleXU=0 Radius=26
  constraints (2):
    c: Coincident(g0,g-1)
    c: Diameter(g0) = 52
FEATURE [PartDesign::Pad] Pad008
  Direction = (0,0,1)
  Length = 20
  Length2 = 10
  Profile = -> Sketch015
  ReferenceAxis = -> Sketch015 [N_Axis]
  Type = 0
FEATURE [PartDesign::Body] Body008  label="Foam1"
  Group = -> [Sketch015,Pad008]
  Origin = -> Origin008
  Placement = pos=(0,0,38) rot=(0,0,1;0rad)
  Tip = -> Pad008
FEATURE [PartDesign::FeatureBase] Clone002
  BaseFeature = -> Body008
  Placement = pos=(0,0,38) rot=(0,0,1;0rad)
FEATURE [PartDesign::Body] Body009  label="Foam2"
  Group = -> [Clone002]
  Origin = -> Origin009
  Placement = pos=(0,0,0) rot=(1,0,0;3.14159rad)
  Tip = -> Clone002
FEATURE [Sketcher::SketchObject] Sketch016
  FullyConstrained = true
  MapMode = 5
  Support = -> [XY_Plane010]
  sketch-geometry (5):
    g0: LineSegment StartX=-22.5 StartY=-0.4 StartZ=0 EndX=-22.5 EndY=0.4 EndZ=0
    g1: LineSegment StartX=-22.5 StartY=0.4 StartZ=0 EndX=22.5 EndY=0.4 EndZ=0
    g2: LineSegment StartX=22.5 StartY=0.4 StartZ=0 EndX=22.5 EndY=-0.4 EndZ=0
    g3: LineSegment StartX=22.5 StartY=-0.4 StartZ=0 EndX=-22.5 EndY=-0.4 EndZ=0
    g4: GeomPoint X=0 Y=0 Z=0
  constraints (12):
    c: Coincident(g0,g1)
    c: Coincident(g1,g2)
    c: Coincident(g2,g3)
    c: Coincident(g3,g0)
    c: Horizontal(g1)
    c: Horizontal(g3)
    c: Vertical(g0)
    c: Vertical(g2)
    c: Symmetric(g1,g0,g4)
    c: Coincident(g4,g-1)
    c: DistanceX(g1,g1) = 45
    c: DistanceY(g2,g2) = 0.8
FEATURE [PartDesign::Pad] Pad009
  Direction = (0,0,1)
  Length = 9
  Length2 = 9
  Profile = -> Sketch016
  ReferenceAxis = -> Sketch016 [N_Axis]
  Type = 4
FEATURE [PartDesign::Body] Body010  label="ShimStock"
  Group = -> [Sketch016,Pad009]
  Origin = -> Origin010
  Placement = pos=(0,11,0) rot=(0,0,1;0rad)
  Tip = -> Pad009
FEATURE [Sketcher::SketchObject] Sketch017
  FullyConstrained = true
  MapMode = 5
  Placement = pos=(0,0,0) rot=(1,0,0;1.5708rad)
  Support = -> [XZ_Plane011]
  sketch-geometry (1):
    g0: Circle CenterX=0 CenterY=0 CenterZ=0 NormalX=0 NormalY=0 NormalZ=1 AngleXU=0 Radius=5
  constraints (2):
    c: Coincident(g0,g-1)
    c: Diameter(g0) = 10
FEATURE [PartDesign::Pad] Pad010
  Direction = (0,-1,-2e-16)
  Length = 3
  Length2 = 10
  Placement = pos=(0,0,0) rot=(1,0,0;1.5708rad)
  Profile = -> Sketch017
  ReferenceAxis = -> Sketch017 [N_Axis]
  Type = 0
FEATURE [PartDesign::Body] Body011  label="TopFoam"
  Group = -> [Sketch017,Pad010]
  Origin = -> Origin011
  Placement = pos=(0,15,0) rot=(0,0,1;0rad)
  Tip = -> Pad010
FEATURE [Sketcher::SketchObject] Sketch018
  FullyConstrained = false
  MapMode = 5
  Support = -> [XY_Plane003]
  sketch-geometry (1):
    g0: Circle CenterX=0 CenterY=-15.4348 CenterZ=0 NormalX=0 NormalY=0 NormalZ=1 AngleXU=0 Radius=4
  constraints (2):
    c: PointOnObject(g0,g-2)
    c: Diameter(g0) = 8
FEATURE [PartDesign::Pocket] Pocket008
  BaseFeature = -> Pad003
  Direction = (0,0,-1)
  Length = 50
  Length2 = 50
  Placement = pos=(0,0,0) rot=(1,0,0;1.5708rad)
  Profile = -> Sketch018
  ReferenceAxis = -> Sketch018 [N_Axis]
  Type = 4
FEATURE [Sketcher::SketchObject] Sketch019
  FullyConstrained = true
  MapMode = 5
  Placement = pos=(0,0,0) rot=(1,0,0;1.5708rad)
  Support = -> [XZ_Plane003]
  sketch-geometry (17):
    g0: LineSegment StartX=12 StartY=-2 StartZ=0 EndX=12 EndY=2 EndZ=0
    g1: LineSegment StartX=12 StartY=2 StartZ=0 EndX=2 EndY=2 EndZ=0
    g2: LineSegment StartX=2 StartY=2 StartZ=0 EndX=2 EndY=12 EndZ=0
    g3: LineSegment StartX=2 StartY=12 StartZ=0 EndX=-2 EndY=12 EndZ=0
    g4: LineSegment StartX=-2 StartY=12 StartZ=0 EndX=-2 EndY=2 EndZ=0
    g5: LineSegment StartX=-2 StartY=2 StartZ=0 EndX=-12 EndY=2 EndZ=0
    g6: LineSegment StartX=-12 StartY=2 StartZ=0 EndX=-12 EndY=-2 EndZ=0
    g7: LineSegment StartX=-12 StartY=-2 StartZ=0 EndX=-2 EndY=-2 EndZ=0
    g8: LineSegment StartX=-2 StartY=-2 StartZ=0 EndX=-2 EndY=-12 EndZ=0
    g9: LineSegment StartX=-2 StartY=-12 StartZ=0 EndX=2 EndY=-12 EndZ=0
    g10: LineSegment StartX=2 StartY=-12 StartZ=0 EndX=2 EndY=-2 EndZ=0
    g11: LineSegment StartX=2 StartY=-2 StartZ=0 EndX=12 EndY=-2 EndZ=0
    g12: LineSegment StartX=-2 StartY=-2 StartZ=0 EndX=-2 EndY=2 EndZ=0
    g13: LineSegment StartX=-2 StartY=2 StartZ=0 EndX=2 EndY=2 EndZ=0
    g14: LineSegment StartX=2 StartY=2 StartZ=0 EndX=2 EndY=-2 EndZ=0
    g15: LineSegment StartX=2 StartY=-2 StartZ=0 EndX=-2 EndY=-2 EndZ=0
    g16: GeomPoint X=0 Y=0 Z=0
  constraints (46):
    c: Vertical(g0)
    c: Coincident(g1,g0)
    c: Horizontal(g1)
    c: Coincident(g2,g1)
    c: Vertical(g2)
    c: Coincident(g3,g2)
    c: Horizontal(g3)
    c: Coincident(g4,g3)
    c: Vertical(g4)
    c: Coincident(g5,g4)
    c: Horizontal(g5)
    c: Coincident(g6,g5)
    c: Vertical(g6)
    c: Horizontal(g7)
    c: Coincident(g8,g7)
    c: Vertical(g8)
    c: Horizontal(g9)
    c: Coincident(g10,g9)
    c: Vertical(g10)
    c: Coincident(g11,g10)
    c: Coincident(g11,g0)
    c: Horizontal(g11)
    c: Equal(g0,g3)
    c: Equal(g3,g6)
    c: Equal(g6,g9)
    c: Coincident(g6,g7)
    c: Coincident(g9,g8)
    c: Equal(g11,g7)
    c: Equal(g11,g1)
    c: Equal(g2,g4)
    c: Equal(g5,g10)
    c: Coincident(g12,g13)
    c: Coincident(g13,g14)
    c: Coincident(g14,g15)
    c: Coincident(g15,g12)
    c: Horizontal(g13)
    c: Horizontal(g15)
    c: Vertical(g12)
    c: Vertical(g14)
    c: Symmetric(g13,g12,g16)
    c: Coincident(g16,g-1)
    c: Coincident(g13,g1)
    c: Coincident(g7,g12)
    c: DistanceX(g13,g13) = 4
    c: DistanceY(g2,g2) = 10
    c: Equal(g10,g2)
FEATURE [PartDesign::Pocket] Pocket009
  BaseFeature = -> Pocket008
  Direction = (0,1,2e-16)
  Length = 3
  Length2 = 5
  Placement = pos=(0,0,0) rot=(1,0,0;1.5708rad)
  Profile = -> Sketch019
  ReferenceAxis = -> Sketch019 [N_Axis]
  Reversed = true
  Type = 0
FEATURE [PartDesign::Body] Body003  label="MetalHandle"
  Group = -> [Sketch011,Pad003,Sketch018,Pocket008,Sketch019,Pocket009]
  Origin = -> Origin003
  Placement = pos=(0,2.5,0) rot=(0,0,1;0rad)
  Tip = -> Pocket009
FEATURE [Sketcher::SketchObject] Sketch020
  FullyConstrained = true
  MapMode = 5
  Placement = pos=(0,0,0) rot=(1,0,0;1.5708rad)
  Support = -> [XZ_Plane012]
  expr: Constraints[43] = Sketch019.Constraints[43]
  expr: Constraints[44] = Sketch019.Constraints[44]
  expr: Constraints[77] = <<Properties>>.Clearance
  expr: Constraints[78] = <<Properties>>.Clearance
  expr: Constraints[79] = <<Properties>>.Clearance
  expr: Constraints[81] = (<<Properties>>.Handle_OD + 2) / 2 - <<Properties>>.Clearance
  sketch-geometry (29):
    g0: LineSegment StartX=12 StartY=-2 StartZ=0 EndX=12 EndY=2 EndZ=0
    g1: LineSegment StartX=12 StartY=2 StartZ=0 EndX=2 EndY=2 EndZ=0
    g2: LineSegment StartX=2 StartY=2 StartZ=0 EndX=2 EndY=12 EndZ=0
    g3: LineSegment StartX=2 StartY=12 StartZ=0 EndX=-2 EndY=12 EndZ=0
    g4: LineSegment StartX=-2 StartY=12 StartZ=0 EndX=-2 EndY=2 EndZ=0
    g5: LineSegment StartX=-2 StartY=2 StartZ=0 EndX=-12 EndY=2 EndZ=0
    g6: LineSegment StartX=-12 StartY=2 StartZ=0 EndX=-12 EndY=-2 EndZ=0
    g7: LineSegment StartX=-12 StartY=-2 StartZ=0 EndX=-2 EndY=-2 EndZ=0
    g8: LineSegment StartX=-2 StartY=-2 StartZ=0 EndX=-2 EndY=-12 EndZ=0
    g9: LineSegment StartX=-2 StartY=-12 StartZ=0 EndX=2 EndY=-12 EndZ=0
    g10: LineSegment StartX=2 StartY=-12 StartZ=0 EndX=2 EndY=-2 EndZ=0
    g11: LineSegment StartX=2 StartY=-2 StartZ=0 EndX=12 EndY=-2 EndZ=0
    g12: LineSegment StartX=-2 StartY=-2 StartZ=0 EndX=-2 EndY=2 EndZ=0
    g13: LineSegment StartX=-2 StartY=2 StartZ=0 EndX=2 EndY=2 EndZ=0
    g14: LineSegment StartX=2 StartY=2 StartZ=0 EndX=2 EndY=-2 EndZ=0
    g15: LineSegment StartX=2 StartY=-2 StartZ=0 EndX=-2 EndY=-2 EndZ=0
    g16: GeomPoint X=0 Y=0 Z=0
    g17: LineSegment StartX=-1.8 StartY=11.55 StartZ=0 EndX=-1.8 EndY=1.8 EndZ=0
    g18: LineSegment StartX=-1.8 StartY=1.8 StartZ=0 EndX=-11.55 EndY=1.8 EndZ=0
    g19: LineSegment StartX=-11.55 StartY=1.8 StartZ=0 EndX=-11.55 EndY=-1.8 EndZ=0
    g20: LineSegment StartX=-11.55 StartY=-1.8 StartZ=0 EndX=-1.8 EndY=-1.8 EndZ=0
    g21: LineSegment StartX=-1.8 StartY=-1.8 StartZ=0 EndX=-1.8 EndY=-11.55 EndZ=0
    g22: LineSegment StartX=-1.8 StartY=-11.55 StartZ=0 EndX=1.8 EndY=-11.55 EndZ=0
    g23: LineSegment StartX=1.8 StartY=-11.55 StartZ=0 EndX=1.8 EndY=-1.8 EndZ=0
    g24: LineSegment StartX=1.8 StartY=-1.8 StartZ=0 EndX=11.55 EndY=-1.8 EndZ=0
    g25: LineSegment StartX=11.55 StartY=-1.8 StartZ=0 EndX=11.55 EndY=1.8 EndZ=0
    g26: LineSegment StartX=11.55 StartY=1.8 StartZ=0 EndX=1.8 EndY=1.8 EndZ=0
    g27: LineSegment StartX=1.8 StartY=1.8 StartZ=0 EndX=1.8 EndY=11.55 EndZ=0
    g28: LineSegment StartX=1.8 StartY=11.55 StartZ=0 EndX=-1.8 EndY=11.55 EndZ=0
  constraints (82):
    c: Vertical(g0)
    c: Coincident(g1,g0)
    c: Horizontal(g1)
    c: Coincident(g2,g1)
    c: Vertical(g2)
    c: Coincident(g3,g2)
    c: Horizontal(g3)
    c: Coincident(g4,g3)
    c: Vertical(g4)
    c: Coincident(g5,g4)
    c: Horizontal(g5)
    c: Coincident(g6,g5)
    c: Vertical(g6)
    c: Horizontal(g7)
    c: Coincident(g8,g7)
    c: Vertical(g8)
    c: Horizontal(g9)
    c: Coincident(g10,g9)
    c: Vertical(g10)
    c: Coincident(g11,g10)
    c: Coincident(g11,g0)
    c: Horizontal(g11)
    c: Equal(g0,g3)
    c: Equal(g3,g6)
    c: Equal(g6,g9)
    c: Coincident(g6,g7)
    c: Coincident(g9,g8)
    c: Equal(g11,g7)
    c: Equal(g11,g1)
    c: Equal(g2,g4)
    c: Equal(g5,g10)
    c: Coincident(g12,g13)
    c: Coincident(g13,g14)
    c: Coincident(g14,g15)
    c: Coincident(g15,g12)
    c: Horizontal(g13)
    c: Horizontal(g15)
    c: Vertical(g12)
    c: Vertical(g14)
    c: Symmetric(g13,g12,g16)
    c: Coincident(g16,g-1)
    c: Coincident(g13,g1)
    c: Coincident(g7,g12)
    c: DistanceX(g13,g13) = 4
    c: DistanceY(g2,g2) = 10
    c: Equal(g10,g2)
    c: Vertical(g17)
    c: Coincident(g18,g17)
    c: Horizontal(g18)
    c: Coincident(g19,g18)
    c: Vertical(g19)
    c: Coincident(g20,g19)
    c: Horizontal(g20)
    c: Coincident(g21,g20)
    c: Vertical(g21)
    c: Coincident(g22,g21)
    c: Horizontal(g22)
    c: Coincident(g23,g22)
    c: Vertical(g23)
    c: Coincident(g24,g23)
    c: Horizontal(g24)
    c: Coincident(g25,g24)
    c: Vertical(g25)
    c: Coincident(g26,g25)
    c: Horizontal(g26)
    c: Coincident(g27,g26)
    c: Vertical(g27)
    c: Coincident(g28,g27)
    c: Coincident(g28,g17)
    c: Horizontal(g28)
    c: Equal(g26,g18)
    c: Equal(g27,g17)
    c: Equal(g26,g24)
    c: Equal(g20,g24)
    c: Equal(g21,g23)
    c: Equal(g23,g27)
    c: Equal(g22,g25)
    c: DistanceX(g26,g1) = 0.2
    c: DistanceY(g26,g1) = 0.2
    c: DistanceY(g0,g24) = 0.2
    c: Equal(g23,g24)
    c: DistanceX(g16,g25) = 11.55
FEATURE [PartDesign::Pad] Pad011
  Direction = (0,-1,2e-16)
  Length = 2.8
  Length2 = 10
  Placement = pos=(0,0,0) rot=(1,0,0;1.5708rad)
  Profile = -> Sketch020
  ReferenceAxis = -> Sketch020 [N_Axis]
  Type = 0
FEATURE [Sketcher::SketchObject] Sketch021
  FullyConstrained = true
  MapMode = 5
  Placement = pos=(0,0,0) rot=(1,0,0;1.5708rad)
  Support = -> [XZ_Plane012]
  expr: Constraints[53] = Sketch020.Constraints[43]
  expr: Constraints[54] = Sketch020.Constraints[44]
  expr: Constraints[87] = Sketch020.Constraints[77]
  expr: Constraints[88] = Sketch020.Constraints[78]
  expr: Constraints[89] = Sketch020.Constraints[79]
  expr: Constraints[91] = Sketch020.Constraints[81]
  sketch-geometry (34):
    g0: LineSegment StartX=11.55 StartY=11.55 StartZ=0 EndX=11.55 EndY=-11.55 EndZ=0
    g1: LineSegment StartX=11.55 StartY=-11.55 StartZ=0 EndX=-11.55 EndY=-11.55 EndZ=0
    g2: LineSegment StartX=-11.55 StartY=-11.55 StartZ=0 EndX=-11.55 EndY=11.55 EndZ=0
    g3: LineSegment StartX=-11.55 StartY=11.55 StartZ=0 EndX=11.55 EndY=11.55 EndZ=0
    g4: GeomPoint X=0 Y=0 Z=0
    g5: LineSegment StartX=12 StartY=-2 StartZ=0 EndX=12 EndY=2 EndZ=0
    g6: LineSegment StartX=12 StartY=2 StartZ=0 EndX=2 EndY=2 EndZ=0
    g7: LineSegment StartX=2 StartY=2 StartZ=0 EndX=2 EndY=12 EndZ=0
    g8: LineSegment StartX=2 StartY=12 StartZ=0 EndX=-2 EndY=12 EndZ=0
    g9: LineSegment StartX=-2 StartY=12 StartZ=0 EndX=-2 EndY=2 EndZ=0
    g10: LineSegment StartX=-2 StartY=2 StartZ=0 EndX=-12 EndY=2 EndZ=0
    g11: LineSegment StartX=-12 StartY=2 StartZ=0 EndX=-12 EndY=-2 EndZ=0
    g12: LineSegment StartX=-12 StartY=-2 StartZ=0 EndX=-2 EndY=-2 EndZ=0
    g13: LineSegment StartX=-2 StartY=-2 StartZ=0 EndX=-2 EndY=-12 EndZ=0
    g14: LineSegment StartX=-2 StartY=-12 StartZ=0 EndX=2 EndY=-12 EndZ=0
    g15: LineSegment StartX=2 StartY=-12 StartZ=0 EndX=2 EndY=-2 EndZ=0
    g16: LineSegment StartX=2 StartY=-2 StartZ=0 EndX=12 EndY=-2 EndZ=0
    g17: LineSegment StartX=-2 StartY=-2 StartZ=0 EndX=-2 EndY=2 EndZ=0
    g18: LineSegment StartX=-2 StartY=2 StartZ=0 EndX=2 EndY=2 EndZ=0
    g19: LineSegment StartX=2 StartY=2 StartZ=0 EndX=2 EndY=-2 EndZ=0
    g20: LineSegment StartX=2 StartY=-2 StartZ=0 EndX=-2 EndY=-2 EndZ=0
    g21: GeomPoint X=0 Y=0 Z=0
    g22: LineSegment StartX=-1.8 StartY=11.55 StartZ=0 EndX=-1.8 EndY=1.8 EndZ=0
    g23: LineSegment StartX=-1.8 StartY=1.8 StartZ=0 EndX=-11.55 EndY=1.8 EndZ=0
    g24: LineSegment StartX=-11.55 StartY=1.8 StartZ=0 EndX=-11.55 EndY=-1.8 EndZ=0
    g25: LineSegment StartX=-11.55 StartY=-1.8 StartZ=0 EndX=-1.8 EndY=-1.8 EndZ=0
    g26: LineSegment StartX=-1.8 StartY=-1.8 StartZ=0 EndX=-1.8 EndY=-11.55 EndZ=0
    g27: LineSegment StartX=-1.8 StartY=-11.55 StartZ=0 EndX=1.8 EndY=-11.55 EndZ=0
    g28: LineSegment StartX=1.8 StartY=-11.55 StartZ=0 EndX=1.8 EndY=-1.8 EndZ=0
    g29: LineSegment StartX=1.8 StartY=-1.8 StartZ=0 EndX=11.55 EndY=-1.8 EndZ=0
    g30: LineSegment StartX=11.55 StartY=-1.8 StartZ=0 EndX=11.55 EndY=1.8 EndZ=0
    g31: LineSegment StartX=11.55 StartY=1.8 StartZ=0 EndX=1.8 EndY=1.8 EndZ=0
    g32: LineSegment StartX=1.8 StartY=1.8 StartZ=0 EndX=1.8 EndY=11.55 EndZ=0
    g33: LineSegment StartX=1.8 StartY=11.55 StartZ=0 EndX=-1.8 EndY=11.55 EndZ=0
  constraints (94):
    c: Coincident(g0,g1)
    c: Coincident(g1,g2)
    c: Coincident(g2,g3)
    c: Coincident(g3,g0)
    c: Horizontal(g1)
    c: Horizontal(g3)
    c: Vertical(g0)
    c: Vertical(g2)
    c: Symmetric(g1,g0,g4)
    c: Coincident(g4,g-1)
    c: Vertical(g5)
    c: Coincident(g6,g5)
    c: Horizontal(g6)
    c: Coincident(g7,g6)
    c: Vertical(g7)
    c: Coincident(g8,g7)
    c: Horizontal(g8)
    c: Coincident(g9,g8)
    c: Vertical(g9)
    c: Coincident(g10,g9)
    c: Horizontal(g10)
    c: Coincident(g11,g10)
    c: Vertical(g11)
    c: Horizontal(g12)
    c: Coincident(g13,g12)
    c: Vertical(g13)
    c: Horizontal(g14)
    c: Coincident(g15,g14)
    c: Vertical(g15)
    c: Coincident(g16,g15)
    c: Coincident(g16,g5)
    c: Horizontal(g16)
    c: Equal(g5,g8)
    c: Equal(g8,g11)
    c: Equal(g11,g14)
    c: Coincident(g11,g12)
    c: Coincident(g14,g13)
    c: Equal(g16,g12)
    c: Equal(g16,g6)
    c: Equal(g7,g9)
    c: Equal(g10,g15)
    c: Coincident(g17,g18)
    c: Coincident(g18,g19)
    c: Coincident(g19,g20)
    c: Coincident(g20,g17)
    c: Horizontal(g18)
    c: Horizontal(g20)
    c: Vertical(g17)
    c: Vertical(g19)
    c: Symmetric(g18,g17,g21)
    c: Coincident(g21,g-1)
    c: Coincident(g18,g6)
    c: Coincident(g12,g17)
    c: DistanceX(g18,g18) = 4
    c: DistanceY(g7,g7) = 10
    c: Equal(g15,g7)
    c: Vertical(g22)
    c: Coincident(g23,g22)
    c: Horizontal(g23)
    c: Coincident(g24,g23)
    c: Vertical(g24)
    c: Coincident(g25,g24)
    c: Horizontal(g25)
    c: Coincident(g26,g25)
    c: Vertical(g26)
    c: Coincident(g27,g26)
    c: Horizontal(g27)
    c: Coincident(g28,g27)
    c: Vertical(g28)
    c: Coincident(g29,g28)
    c: Horizontal(g29)
    c: Coincident(g30,g29)
    c: Vertical(g30)
    c: Coincident(g31,g30)
    c: Horizontal(g31)
    c: Coincident(g32,g31)
    c: Vertical(g32)
    c: Coincident(g33,g32)
    c: Coincident(g33,g22)
    c: Horizontal(g33)
    c: Equal(g31,g23)
    c: Equal(g32,g22)
    c: Equal(g31,g29)
    c: Equal(g25,g29)
    c: Equal(g26,g28)
    c: Equal(g28,g32)
    c: Equal(g27,g30)
    c: DistanceX(g31,g6) = 0.2
    c: DistanceY(g31,g6) = 0.2
    c: DistanceY(g5,g29) = 0.2
    c: Equal(g28,g29)
    c: DistanceX(g21,g30) = 11.55
    c: PointOnObject(g22,g3)
    c: PointOnObject(g23,g2)
FEATURE [PartDesign::Pad] Pad012
  BaseFeature = -> Pad011
  Direction = (0,-1,2e-16)
  Length = 5
  Length2 = 10
  Placement = pos=(0,0,0) rot=(1,0,0;1.5708rad)
  Profile = -> Sketch021
  ReferenceAxis = -> Sketch021 [N_Axis]
  Reversed = true
  Type = 0
FEATURE [Sketcher::SketchObject] Sketch022
  ExternalGeometry = -> [Cone001]
  FullyConstrained = true
  MapMode = 5
  Placement = pos=(2.3e-15,10.5,-35) rot=(-1,0,0;1.5708rad)
  Support = -> [Cone001]
  expr: Constraints[11] = <<Properties>>.Handle_OD + 2
  sketch-geometry (5):
    g0: LineSegment StartX=-11.75 StartY=-46.75 StartZ=0 EndX=-11.75 EndY=-23.25 EndZ=0
    g1: LineSegment StartX=-11.75 StartY=-23.25 StartZ=0 EndX=11.75 EndY=-23.25 EndZ=0
    g2: LineSegment StartX=11.75 StartY=-23.25 StartZ=0 EndX=11.75 EndY=-46.75 EndZ=0
    g3: LineSegment StartX=11.75 StartY=-46.75 StartZ=0 EndX=-11.75 EndY=-46.75 EndZ=0
    g4: GeomPoint X=-2.3e-15 Y=-35 Z=0
  constraints (12):
    c: Coincident(g0,g1)
    c: Coincident(g1,g2)
    c: Coincident(g2,g3)
    c: Coincident(g3,g0)
    c: Horizontal(g1)
    c: Horizontal(g3)
    c: Vertical(g0)
    c: Vertical(g2)
    c: Symmetric(g1,g0,g4)
    c: Coincident(g4,g-3)
    c: Equal(g2,g1)
    c: DistanceX(g1,g1) = 23.5
FEATURE [PartDesign::Pocket] Pocket010
  BaseFeature = -> Cone001
  Direction = (-2e-16,-1,2e-16)
  Length = 8
  Length2 = 5
  Placement = pos=(0,0,-35) rot=(1,0,0;3.14159rad)
  Profile = -> Sketch022
  ReferenceAxis = -> Sketch022 [N_Axis]
  Type = 0
FEATURE [Sketcher::SketchObject] Sketch023
  FullyConstrained = true
  MapMode = 5
  Placement = pos=(0,5,-2.2e-15) rot=(-1,0,0;1.5708rad)
  Support = -> [Pad012]
  sketch-geometry (1):
    g0: Circle CenterX=0 CenterY=0 CenterZ=0 NormalX=0 NormalY=0 NormalZ=1 AngleXU=0 Radius=2.5
  constraints (2):
    c: Coincident(g0,g-1)
    c: Diameter(g0) = 5
FEATURE [PartDesign::Pad] Pad013
  BaseFeature = -> Pad012
  Direction = (0,1,-2e-16)
  Length = 3
  Length2 = 10
  Placement = pos=(0,0,0) rot=(1,0,0;1.5708rad)
  Profile = -> Sketch023
  ReferenceAxis = -> Sketch023 [N_Axis]
  Type = 0
FEATURE [PartDesign::Fillet] Fillet
  Base = -> Pad013 [Edge51]
  BaseFeature = -> Pad013
  Placement = pos=(0,0,0) rot=(1,0,0;1.5708rad)
  Radius = 2
  SupportTransform = false
  UseAllEdges = false
FEATURE [Sketcher::SketchObject] Sketch024
  ExternalGeometry = -> [Cone001]
  FullyConstrained = true
  MapMode = 5
  Placement = pos=(6e-16,2.5,-35) rot=(-1,0,0;1.5708rad)
  Support = -> [Pocket010]
  expr: Constraints[11] = Sketch022.Constraints[11]
  expr: Constraints[54] = Sketch019.Constraints[43]
  expr: Constraints[55] = Sketch019.Constraints[44]
  sketch-geometry (34):
    g0: LineSegment StartX=-11.75 StartY=-46.75 StartZ=0 EndX=-11.75 EndY=-23.25 EndZ=0
    g1: LineSegment StartX=-11.75 StartY=-23.25 StartZ=0 EndX=11.75 EndY=-23.25 EndZ=0
    g2: LineSegment StartX=11.75 StartY=-23.25 StartZ=0 EndX=11.75 EndY=-46.75 EndZ=0
    g3: LineSegment StartX=11.75 StartY=-46.75 StartZ=0 EndX=-11.75 EndY=-46.75 EndZ=0
    g4: GeomPoint X=-2.4e-15 Y=-35 Z=0
    g5: LineSegment StartX=12 StartY=-37 StartZ=0 EndX=12 EndY=-33 EndZ=0
    g6: LineSegment StartX=12 StartY=-33 StartZ=0 EndX=2 EndY=-33 EndZ=0
    g7: LineSegment StartX=2 StartY=-33 StartZ=0 EndX=2 EndY=-23 EndZ=0
    g8: LineSegment StartX=2 StartY=-23 StartZ=0 EndX=-2 EndY=-23 EndZ=0
    g9: LineSegment StartX=-2 StartY=-23 StartZ=0 EndX=-2 EndY=-33 EndZ=0
    g10: LineSegment StartX=-2 StartY=-33 StartZ=0 EndX=-12 EndY=-33 EndZ=0
    g11: LineSegment StartX=-12 StartY=-33 StartZ=0 EndX=-12 EndY=-37 EndZ=0
    g12: LineSegment StartX=-12 StartY=-37 StartZ=0 EndX=-2 EndY=-37 EndZ=0
    g13: LineSegment StartX=-2 StartY=-37 StartZ=0 EndX=-2 EndY=-47 EndZ=0
    g14: LineSegment StartX=-2 StartY=-47 StartZ=0 EndX=2 EndY=-47 EndZ=0
    g15: LineSegment StartX=2 StartY=-47 StartZ=0 EndX=2 EndY=-37 EndZ=0
    g16: LineSegment StartX=2 StartY=-37 StartZ=0 EndX=12 EndY=-37 EndZ=0
    g17: LineSegment StartX=-2 StartY=-37 StartZ=0 EndX=-2 EndY=-33 EndZ=0
    g18: LineSegment StartX=-2 StartY=-33 StartZ=0 EndX=2 EndY=-33 EndZ=0
    g19: LineSegment StartX=2 StartY=-33 StartZ=0 EndX=2 EndY=-37 EndZ=0
    g20: LineSegment StartX=2 StartY=-37 StartZ=0 EndX=-2 EndY=-37 EndZ=0
    g21: GeomPoint X=0 Y=0 Z=0
    g22: LineSegment StartX=-2 StartY=-23.25 StartZ=0 EndX=2 EndY=-23.25 EndZ=0
    g23: LineSegment StartX=2 StartY=-23.25 StartZ=0 EndX=2 EndY=-33 EndZ=0
    g24: LineSegment StartX=2 StartY=-33 StartZ=0 EndX=11.75 EndY=-33 EndZ=0
    g25: LineSegment StartX=11.75 StartY=-33 StartZ=0 EndX=11.75 EndY=-37 EndZ=0
    g26: LineSegment StartX=11.75 StartY=-37 StartZ=0 EndX=2 EndY=-37 EndZ=0
    g27: LineSegment StartX=2 StartY=-37 StartZ=0 EndX=2 EndY=-46.75 EndZ=0
    g28: LineSegment StartX=2 StartY=-46.75 StartZ=0 EndX=-2 EndY=-46.75 EndZ=0
    g29: LineSegment StartX=-2 StartY=-46.75 StartZ=0 EndX=-2 EndY=-37 EndZ=0
    g30: LineSegment StartX=-2 StartY=-37 StartZ=0 EndX=-11.75 EndY=-37 EndZ=0
    g31: LineSegment StartX=-11.75 StartY=-37 StartZ=0 EndX=-11.75 EndY=-33 EndZ=0
    g32: LineSegment StartX=-11.75 StartY=-33 StartZ=0 EndX=-2 EndY=-33 EndZ=0
    g33: LineSegment StartX=-2 StartY=-33 StartZ=0 EndX=-2 EndY=-23.25 EndZ=0
  constraints (90):
    c: Coincident(g0,g1)
    c: Coincident(g1,g2)
    c: Coincident(g2,g3)
    c: Coincident(g3,g0)
    c: Horizontal(g1)
    c: Horizontal(g3)
    c: Vertical(g0)
    c: Vertical(g2)
    c: Symmetric(g1,g0,g4)
    c: Coincident(g4,g-3)
    c: Equal(g2,g1)
    c: DistanceX(g1,g1) = 23.5
    c: Vertical(g5)
    c: Coincident(g6,g5)
    c: Horizontal(g6)
    c: Coincident(g7,g6)
    c: Vertical(g7)
    c: Coincident(g8,g7)
    c: Horizontal(g8)
    c: Coincident(g9,g8)
    c: Vertical(g9)
    c: Coincident(g10,g9)
    c: Horizontal(g10)
    c: Coincident(g11,g10)
    c: Vertical(g11)
    c: Horizontal(g12)
    c: Coincident(g13,g12)
    c: Vertical(g13)
    c: Horizontal(g14)
    c: Coincident(g15,g14)
    c: Vertical(g15)
    c: Coincident(g16,g15)
    c: Coincident(g16,g5)
    c: Horizontal(g16)
    c: Equal(g5,g8)
    c: Equal(g8,g11)
    c: Equal(g11,g14)
    c: Coincident(g11,g12)
    c: Coincident(g14,g13)
    c: Equal(g16,g12)
    c: Equal(g16,g6)
    c: Equal(g7,g9)
    c: Equal(g10,g15)
    c: Coincident(g17,g18)
    c: Coincident(g18,g19)
    c: Coincident(g19,g20)
    c: Coincident(g20,g17)
    c: Horizontal(g18)
    c: Horizontal(g20)
    c: Vertical(g17)
    c: Vertical(g19)
    c: Coincident(g21,g-1)
    c: Coincident(g18,g6)
    c: Coincident(g12,g17)
    c: DistanceX(g18,g18) = 4
    c: DistanceY(g7,g7) = 10
    c: Equal(g15,g7)
    c: Symmetric(g6,g12,g4)
    c: PointOnObject(g22,g9)
    c: PointOnObject(g22,g1)
    c: Horizontal(g22)
    c: PointOnObject(g22,g7)
    c: Coincident(g23,g22)
    c: Coincident(g23,g6)
    c: Coincident(g24,g23)
    c: PointOnObject(g24,g2)
    c: Horizontal(g24)
    c: Coincident(g25,g24)
    c: PointOnObject(g25,g16)
    c: Vertical(g25)
    c: Coincident(g26,g25)
    c: Coincident(g26,g15)
    c: Coincident(g27,g26)
    c: PointOnObject(g27,g3)
    c: Vertical(g27)
    c: Coincident(g28,g27)
    c: PointOnObject(g28,g13)
    c: Horizontal(g28)
    c: Coincident(g29,g28)
    c: Coincident(g29,g12)
    c: Coincident(g30,g29)
    c: PointOnObject(g30,g0)
    c: Horizontal(g30)
    c: Coincident(g31,g30)
    c: PointOnObject(g31,g10)
    c: Vertical(g31)
    c: Coincident(g32,g31)
    c: Coincident(g32,g9)
    c: Coincident(g33,g32)
    c: Coincident(g33,g22)
FEATURE [PartDesign::Pocket] Pocket011
  BaseFeature = -> Pocket010
  Direction = (-2e-16,-1,2e-16)
  Length = 3
  Length2 = 5
  Placement = pos=(0,0,-35) rot=(1,0,0;3.14159rad)
  Profile = -> Sketch024
  ReferenceAxis = -> Sketch024 [N_Axis]
  Type = 0
FEATURE [PartDesign::Body] Body  label="HeadInstert"
  Group = -> [Sketch,Pad,Sketch001,Pocket,Sketch002,Pocket001,Sketch004,Pocket002,Chamfer,Sketch003,Pocket003,Chamfer001,Sketch008,Pocket006,Chamfer003,Chamfer004,Chamfer005,Cone,Cone001,Sketch022,Pocket010,Sketch024,Pocket011]
  Origin = -> Origin001
  Tip = -> Pocket011
FEATURE [PartDesign::Fillet] Fillet001
  Base = -> Fillet [Edge3]
  BaseFeature = -> Fillet
  Placement = pos=(0,0,0) rot=(1,0,0;1.5708rad)
  Radius = 7
  SupportTransform = false
  UseAllEdges = false
FEATURE [Sketcher::SketchObject] Sketch025
  FullyConstrained = true
  MapMode = 5
  Placement = pos=(0,0,0) rot=(1,0,0;1.5708rad)
  Support = -> [XZ_Plane012]
  expr: Constraints[1] = <<Properties>>.Handle_OD - <<Properties>>.Clearance * 2
  sketch-geometry (1):
    g0: Circle CenterX=0 CenterY=0 CenterZ=0 NormalX=0 NormalY=0 NormalZ=1 AngleXU=0 Radius=10.55
  constraints (2):
    c: Coincident(g0,g-1)
    c: Diameter(g0) = 21.1
FEATURE [PartDesign::Pad] Pad014
  BaseFeature = -> Fillet001
  Direction = (0,-1,2e-16)
  Length = 9
  Length2 = 10
  Placement = pos=(0,0,0) rot=(1,0,0;1.5708rad)
  Profile = -> Sketch025
  ReferenceAxis = -> Sketch025 [N_Axis]
  TaperAngle = -2
  Type = 0
FEATURE [PartDesign::Chamfer] Chamfer006
  Angle = 45
  Base = -> Pad014 [Edge15,Edge19,Edge10,Edge11]
  BaseFeature = -> Pad014
  ChamferType = 0
  FlipDirection = false
  Placement = pos=(0,0,0) rot=(1,0,0;1.5708rad)
  Size = 1
  Size2 = 1
  SupportTransform = false
  UseAllEdges = false
FEATURE [PartDesign::Body] Body012  label="Pusher"
  Group = -> [Sketch020,Pad011,Sketch021,Pad012,Sketch023,Pad013,Fillet,Fillet001,Sketch025,Pad014,Chamfer006]
  Origin = -> Origin012
  Placement = pos=(0,2.5,0) rot=(0,0,1;0rad)
  Tip = -> Chamfer006
FEATURE [Sketcher::SketchObject] Sketch026
  FullyConstrained = true
  MapMode = 5
  Placement = pos=(0,0,0) rot=(1,0,0;1.5708rad)
  Support = -> [XZ_Plane013]
  expr: Constraints[1] = <<Properties>>.Handle_OD - 1
  sketch-geometry (2):
    g0: Circle CenterX=0 CenterY=0 CenterZ=0 NormalX=0 NormalY=0 NormalZ=1 AngleXU=0 Radius=10.25
    g1: Circle CenterX=0 CenterY=0 CenterZ=0 NormalX=0 NormalY=0 NormalZ=1 AngleXU=0 Radius=4
  constraints (4):
    c: Coincident(g0,g-1)
    c: Diameter(g0) = 20.5
    c: Coincident(g1,g0)
    c: Diameter(g1) = 8
FEATURE [PartDesign::Pad] Pad015
  Direction = (0,-1,-2e-16)
  Length = 10
  Length2 = 10
  Placement = pos=(0,0,0) rot=(1,0,0;1.5708rad)
  Profile = -> Sketch026
  ReferenceAxis = -> Sketch026 [N_Axis]
  Type = 0
FEATURE [PartDesign::Draft] Draft
  Angle = 2
  Base = -> Pad015 [Face1]
  BaseFeature = -> Pad015
  NeutralPlane = -> Pad015 [Face3]
  Placement = pos=(0,0,0) rot=(1,0,0;1.5708rad)
  SupportTransform = false
FEATURE [PartDesign::Body] Body013  label="WirePlug"
  Group = -> [Sketch026,Pad015,Draft]
  Origin = -> Origin013
  Placement = pos=(0,-190,0) rot=(0,0,1;0rad)
  Tip = -> Draft
FEATURE [Sketcher::SketchObject] Sketch027
  FullyConstrained = true
  MapMode = 5
  Placement = pos=(0,0,0) rot=(1,0,0;1.5708rad)
  Support = -> [XZ_Plane002]
  sketch-geometry (5):
    g0: LineSegment StartX=-2.5 StartY=-45 StartZ=0 EndX=-2.5 EndY=45 EndZ=0
    g1: LineSegment StartX=-2.5 StartY=45 StartZ=0 EndX=2.5 EndY=45 EndZ=0
    g2: LineSegment StartX=2.5 StartY=45 StartZ=0 EndX=2.5 EndY=-45 EndZ=0
    g3: LineSegment StartX=2.5 StartY=-45 StartZ=0 EndX=-2.5 EndY=-45 EndZ=0
    g4: GeomPoint X=0 Y=0 Z=0
  constraints (12):
    c: Coincident(g0,g1)
    c: Coincident(g1,g2)
    c: Coincident(g2,g3)
    c: Coincident(g3,g0)
    c: Horizontal(g1)
    c: Horizontal(g3)
    c: Vertical(g0)
    c: Vertical(g2)
    c: Symmetric(g1,g0,g4)
    c: Coincident(g4,g-1)
    c: DistanceX(g1,g1) = 5
    c: DistanceY(g2,g2) = 90
FEATURE [PartDesign::Pocket] Pocket012
  BaseFeature = -> Pocket007
  Direction = (0,1,2e-16)
  Length = 5
  Length2 = 5
  Profile = -> Sketch027
  ReferenceAxis = -> Sketch027 [N_Axis]
  Reversed = true
  Type = 1
FEATURE [PartDesign::Body] Body002  label="PVCHammerHeadShell"
  Group = -> [Sketch009,Pad002,Sketch010,Pocket007,Sketch027,Pocket012]
  Origin = -> Origin002
  Tip = -> Pocket012
